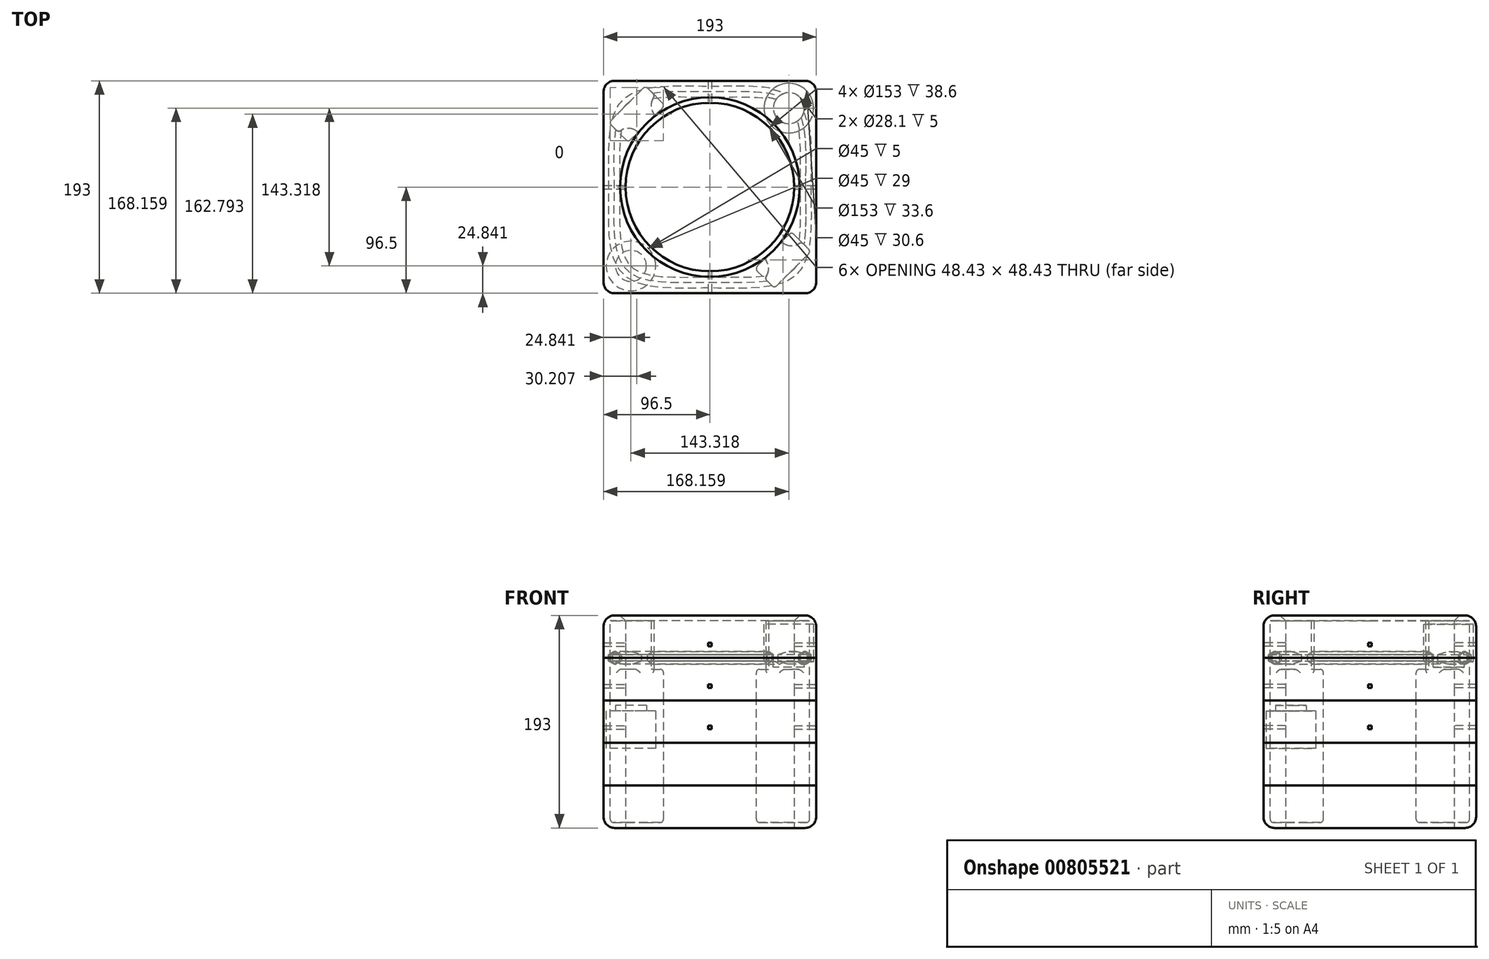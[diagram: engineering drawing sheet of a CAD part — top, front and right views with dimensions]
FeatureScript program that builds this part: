
annotation { "Feature Type Name" : "Feature", "Feature Type Description" : "" }
export const myFeature = defineFeature(function(context is Context, id is Id, definition is map)
    precondition{}
    {
        {
            var Q0;
            Q0=qCreatedBy(makeId("Top.planeOp"),FACE);
            cPlane(context, id + "F0", {"entities" : qUnion([Q0]), "cplaneType" : CPlaneType.OFFSET, "offset" : 0 * mm, "width" : 150 * mm, "height" : 150 * mm});
        }
        {
            var Q0;
            Q0=qCreatedBy(makeId("Top.planeOp"),FACE);
            cPlane(context, id + "F1", {"entities" : qUnion([Q0]), "cplaneType" : CPlaneType.OFFSET, "offset" : 38.6 * mm, "width" : 150 * mm, "height" : 150 * mm});
        }
        {
            var Q0;
            Q0=qCreatedBy(makeId("Top.planeOp"),FACE);
            cPlane(context, id + "F2", {"entities" : qUnion([Q0]), "cplaneType" : CPlaneType.OFFSET, "offset" : 77.2 * mm, "width" : 150 * mm, "height" : 150 * mm});
        }
        {
            var Q0;
            Q0=qCreatedBy(makeId("Top.planeOp"),FACE);
            cPlane(context, id + "F3", {"entities" : qUnion([Q0]), "cplaneType" : CPlaneType.OFFSET, "offset" : 115.8 * mm, "width" : 150 * mm, "height" : 150 * mm});
        }
        {
            var Q0;
            Q0=qCreatedBy(makeId("Top.planeOp"),FACE);
            cPlane(context, id + "F4", {"entities" : qUnion([Q0]), "cplaneType" : CPlaneType.OFFSET, "offset" : 154.4 * mm, "width" : 150 * mm, "height" : 150 * mm});
        }
        {
            var Q0;
            Q0=qCreatedBy(id+"F0.planeOp",FACE);
            cPlane(context, id + "F5", {"entities" : qUnion([Q0]), "cplaneType" : CPlaneType.OFFSET, "offset" : 5 * mm, "width" : 150 * mm, "height" : 150 * mm});
        }
        {
            var Q0;
            Q0=qCreatedBy(id+"F0.planeOp",FACE);
            var sketch = newSketch(context, id + "F6", { "sketchPlane" : qUnion([Q0])});
            skCircle(sketch, "E0", {"center": v(0, 0) * mm, "radius": 76.5 * mm});
            skLineSegment(sketch, "E1.bottom", {"start": v(96.5, 96.5) * mm, "end": v(-96.5, 96.5) * mm});
            skLineSegment(sketch, "E1.top", {"start": v(96.5, -96.5) * mm, "end": v(-96.5, -96.5) * mm});
            skLineSegment(sketch, "E1.left", {"start": v(96.5, 96.5) * mm, "end": v(96.5, -96.5) * mm});
            skLineSegment(sketch, "E1.right", {"start": v(-96.5, 96.5) * mm, "end": v(-96.5, -96.5) * mm});
            skLineSegment(sketch, "E2", {"start": v(-76.5, 0) * mm, "end": v(-96.5, 0) * mm, "construction": true});
            skPoint(sketch, "E2.startSnap0", {"position": v(-96.5, 0) * mm});
            skSolve(sketch);
        }
        {
            var Q0;
            Q0=qCreatedBy(id+"F1.planeOp",FACE);
            var sketch = newSketch(context, id + "F7", { "sketchPlane" : qUnion([Q0])});
            skCircle(sketch, "E3", {"center": v(0, 0) * mm, "radius": 76.5 * mm});
            skLineSegment(sketch, "E4.bottom", {"start": v(96.5, 96.5) * mm, "end": v(-96.5, 96.5) * mm});
            skLineSegment(sketch, "E4.top", {"start": v(96.5, -96.5) * mm, "end": v(-96.5, -96.5) * mm});
            skLineSegment(sketch, "E4.left", {"start": v(96.5, 96.5) * mm, "end": v(96.5, -96.5) * mm});
            skLineSegment(sketch, "E4.right", {"start": v(-96.5, 96.5) * mm, "end": v(-96.5, -96.5) * mm});
            skLineSegment(sketch, "E5", {"start": v(-76.5, 0) * mm, "end": v(-96.5, 0) * mm, "construction": true});
            skPoint(sketch, "E5.startSnap0", {"position": v(-96.5, 0) * mm});
            skSolve(sketch);
        }
        {
            var Q0;
            Q0=qCreatedBy(id+"F2.planeOp",FACE);
            var sketch = newSketch(context, id + "F8", { "sketchPlane" : qUnion([Q0])});
            skCircle(sketch, "E6", {"center": v(0, 0) * mm, "radius": 76.5 * mm});
            skLineSegment(sketch, "E7.bottom", {"start": v(96.5, 96.5) * mm, "end": v(-96.5, 96.5) * mm});
            skLineSegment(sketch, "E7.top", {"start": v(96.5, -96.5) * mm, "end": v(-96.5, -96.5) * mm});
            skLineSegment(sketch, "E7.left", {"start": v(96.5, 96.5) * mm, "end": v(96.5, -96.5) * mm});
            skLineSegment(sketch, "E7.right", {"start": v(-96.5, 96.5) * mm, "end": v(-96.5, -96.5) * mm});
            skLineSegment(sketch, "E8", {"start": v(-76.5, 0) * mm, "end": v(-96.5, 0) * mm, "construction": true});
            skPoint(sketch, "E8.startSnap0", {"position": v(-96.5, 0) * mm});
            skSolve(sketch);
        }
        {
            var Q0;
            Q0=qCreatedBy(id+"F3.planeOp",FACE);
            var sketch = newSketch(context, id + "F9", { "sketchPlane" : qUnion([Q0])});
            skCircle(sketch, "E9", {"center": v(0, 0) * mm, "radius": 76.5 * mm});
            skLineSegment(sketch, "E10.bottom", {"start": v(96.5, 96.5) * mm, "end": v(-96.5, 96.5) * mm});
            skLineSegment(sketch, "E10.top", {"start": v(96.5, -96.5) * mm, "end": v(-96.5, -96.5) * mm});
            skLineSegment(sketch, "E10.left", {"start": v(96.5, 96.5) * mm, "end": v(96.5, -96.5) * mm});
            skLineSegment(sketch, "E10.right", {"start": v(-96.5, 96.5) * mm, "end": v(-96.5, -96.5) * mm});
            skLineSegment(sketch, "E11", {"start": v(-76.5, 0) * mm, "end": v(-96.5, 0) * mm, "construction": true});
            skPoint(sketch, "E11.startSnap0", {"position": v(-96.5, 0) * mm});
            skSolve(sketch);
        }
        {
            var Q0;
            Q0=qCreatedBy(id+"F4.planeOp",FACE);
            var sketch = newSketch(context, id + "F10", { "sketchPlane" : qUnion([Q0])});
            skCircle(sketch, "E12", {"center": v(0, 0) * mm, "radius": 76.5 * mm});
            skLineSegment(sketch, "E13.bottom", {"start": v(96.5, 96.5) * mm, "end": v(-96.5, 96.5) * mm});
            skLineSegment(sketch, "E13.top", {"start": v(96.5, -96.5) * mm, "end": v(-96.5, -96.5) * mm});
            skLineSegment(sketch, "E13.left", {"start": v(96.5, 96.5) * mm, "end": v(96.5, -96.5) * mm});
            skLineSegment(sketch, "E13.right", {"start": v(-96.5, 96.5) * mm, "end": v(-96.5, -96.5) * mm});
            skLineSegment(sketch, "E14", {"start": v(-76.5, 0) * mm, "end": v(-96.5, 0) * mm, "construction": true});
            skPoint(sketch, "E14.startSnap0", {"position": v(-96.5, 0) * mm});
            skSolve(sketch);
        }
        {
            var Q0;
            Q0=qCreatedBy(id+"F5.planeOp",FACE);
            var sketch = newSketch(context, id + "F11", { "sketchPlane" : qUnion([Q0])});
            skCircle(sketch, "E15", {"center": v(0, 0) * mm, "radius": 76.5 * mm, "construction": true});
            skLineSegment(sketch, "E16.bottom", {"start": v(96.5, 96.5) * mm, "end": v(-96.5, 96.5) * mm, "construction": true});
            skLineSegment(sketch, "E16.top", {"start": v(96.5, -96.5) * mm, "end": v(-96.5, -96.5) * mm, "construction": true});
            skLineSegment(sketch, "E16.left", {"start": v(96.5, 96.5) * mm, "end": v(96.5, -96.5) * mm, "construction": true});
            skLineSegment(sketch, "E16.right", {"start": v(-96.5, 96.5) * mm, "end": v(-96.5, -96.5) * mm, "construction": true});
            skLineSegment(sketch, "E17", {"start": v(-57.45, 57.45) * mm, "end": v(-40.84, 74.07) * mm});
            skLineSegment(sketch, "E18", {"start": v(-57.45, 57.45) * mm, "end": v(-74.07, 40.84) * mm});
            skLineSegment(sketch, "E19", {"start": v(-74.07, 40.84) * mm, "end": v(-91.75, 58.51) * mm});
            skLineSegment(sketch, "E20", {"start": v(-76.5, 0) * mm, "end": v(-96.5, 0) * mm, "construction": true});
            skLineSegment(sketch, "E21", {"start": v(-91.75, 58.51) * mm, "end": v(-75.13, 75.13) * mm});
            skLineSegment(sketch, "E22", {"start": v(-75.13, 75.13) * mm, "end": v(-58.51, 91.75) * mm});
            skLineSegment(sketch, "E23", {"start": v(-58.51, 91.75) * mm, "end": v(-40.84, 74.07) * mm});
            skLineSegment(sketch, "E24", {"start": v(-91.75, 58.51) * mm, "end": v(-96.5, 58.51) * mm, "construction": true});
            skLineSegment(sketch, "E25", {"start": v(-58.51, 91.75) * mm, "end": v(-58.51, 96.5) * mm, "construction": true});
            skLineSegment(sketch, "E26", {"start": v(57.45, -57.45) * mm, "end": v(74.07, -40.84) * mm});
            skLineSegment(sketch, "E27", {"start": v(57.45, -57.45) * mm, "end": v(40.84, -74.07) * mm});
            skLineSegment(sketch, "E28", {"start": v(40.84, -74.07) * mm, "end": v(58.51, -91.75) * mm});
            skLineSegment(sketch, "E29", {"start": v(91.75, -58.51) * mm, "end": v(74.07, -40.84) * mm});
            skLineSegment(sketch, "E30", {"start": v(91.75, -58.51) * mm, "end": v(96.5, -58.51) * mm, "construction": true});
            skLineSegment(sketch, "E31", {"start": v(58.51, -91.75) * mm, "end": v(75.13, -75.13) * mm});
            skLineSegment(sketch, "E32", {"start": v(75.13, -75.13) * mm, "end": v(91.75, -58.51) * mm});
            skLineSegment(sketch, "E33", {"start": v(-57.45, 57.45) * mm, "end": v(-54.1, 54.1) * mm, "construction": true});
            skLineSegment(sketch, "E34", {"start": v(57.45, -57.45) * mm, "end": v(54.1, -54.1) * mm, "construction": true});
            skLineSegment(sketch, "E35", {"start": v(58.51, -91.75) * mm, "end": v(58.51, -96.5) * mm, "construction": true});
            skLineSegment(sketch, "E36", {"start": v(54.1, -54.1) * mm, "end": v(60.81, -54.1) * mm, "construction": true});
            skLineSegment(sketch, "E37", {"start": v(-54.1, 54.1) * mm, "end": v(-60.81, 54.1) * mm, "construction": true});
            skCircle(sketch, "E38", {"center": v(-74.07, 40.84) * mm, "radius": 12.5 * mm});
            skCircle(sketch, "E39", {"center": v(-40.84, 74.07) * mm, "radius": 12.5 * mm});
            skCircle(sketch, "E40", {"center": v(40.84, -74.07) * mm, "radius": 12.5 * mm});
            skCircle(sketch, "E41", {"center": v(74.07, -40.84) * mm, "radius": 12.5 * mm});
            skSolve(sketch);
        }
        {
            var Q0;
            Q0=makeQuery(id+"F6.imprint","IMPRINT",FACE,{"disambiguationData":[TD([[makeQuery(id+"F6.imprint","IMPRINT",EDGE,{"derivedFrom":sQuery(id+"F6.wireOp",EDGE,"E0")}),-1.0]])]});
            extrude(context, id + "F12", {"entities" : qUnion([Q0]), "depth" : 38.6 * mm, "offsetDistance" : 25 * mm});
        }
        {
            var Q0;
            Q0=makeQuery(id+"F7.imprint","IMPRINT",FACE,{"disambiguationData":[TD([[makeQuery(id+"F7.imprint","IMPRINT",EDGE,{"derivedFrom":sQuery(id+"F7.wireOp",EDGE,"E3")}),-1.0]])]});
            extrude(context, id + "F13", {"entities" : qUnion([Q0]), "depth" : 38.6 * mm, "offsetDistance" : 25 * mm});
        }
        {
            var Q0;
            Q0=makeQuery(id+"F8.imprint","IMPRINT",FACE,{"disambiguationData":[TD([[makeQuery(id+"F8.imprint","IMPRINT",EDGE,{"derivedFrom":sQuery(id+"F8.wireOp",EDGE,"E6")}),-1.0]])]});
            extrude(context, id + "F14", {"entities" : qUnion([Q0]), "depth" : 38.6 * mm, "offsetDistance" : 25 * mm});
        }
        {
            var Q0;
            Q0=makeQuery(id+"F9.imprint","IMPRINT",FACE,{"disambiguationData":[TD([[makeQuery(id+"F9.imprint","IMPRINT",EDGE,{"derivedFrom":sQuery(id+"F9.wireOp",EDGE,"E9")}),-1.0]])]});
            extrude(context, id + "F15", {"entities" : qUnion([Q0]), "depth" : 38.6 * mm, "offsetDistance" : 25 * mm});
        }
        {
            var Q0;
            Q0=makeQuery(id+"F10.imprint","IMPRINT",FACE,{"disambiguationData":[TD([[makeQuery(id+"F10.imprint","IMPRINT",EDGE,{"derivedFrom":sQuery(id+"F10.wireOp",EDGE,"E12")}),-1.0]])]});
            extrude(context, id + "F16", {"entities" : qUnion([Q0]), "depth" : 38.6 * mm, "offsetDistance" : 25 * mm});
        }
        {
            var Q0;
            Q0=makeQuery(id+"F16.opExtrude","CAP_FACE",FACE,{"disambiguationData":[OSD([sQuery(id+"F10.wireOp",EDGE,"E12"),sQuery(id+"F10.wireOp",EDGE,"E13.bottom"),sQuery(id+"F10.wireOp",EDGE,"E13.top"),sQuery(id+"F10.wireOp",EDGE,"E13.left"),sQuery(id+"F10.wireOp",EDGE,"E13.right")])],"isStart":false});
            cPlane(context, id + "F17", {"entities" : qUnion([Q0]), "cplaneType" : CPlaneType.OFFSET, "offset" : 8 * mm, "oppositeDirection" : true, "width" : 150 * mm, "height" : 150 * mm});
        }
        {
            var Q0;
            Q0=qCreatedBy(id+"F2.planeOp",FACE);
            cPlane(context, id + "F18", {"entities" : qUnion([Q0]), "cplaneType" : CPlaneType.OFFSET, "offset" : 5 * mm, "oppositeDirection" : true, "width" : 150 * mm, "height" : 150 * mm});
        }
        {
            var Q0;
            {var subQ0=sQuery(id+"F11.wireOp",EDGE,"E28");var subQ1=sQuery(id+"F11.wireOp",EDGE,"E27");var subQ2=makeQuery(id+"F11.imprint","INTERSECT",VERTEX,{"derivedFrom":[subQ1,subQ0]});Q0=makeQuery(id+"F11.imprint","IMPRINT",FACE,{"disambiguationData":[TD([[makeQuery(id+"F11.imprint","IMPRINT",EDGE,{"disambiguationData":[TD([[subQ2,1.0]])],"derivedFrom":subQ1}),1.0]])]});}
            var Q1;
            {var subQ0=sQuery(id+"F11.wireOp",EDGE,"E29");var subQ1=sQuery(id+"F11.wireOp",EDGE,"E26");var subQ2=makeQuery(id+"F11.imprint","INTERSECT",VERTEX,{"derivedFrom":[subQ1,subQ0]});Q1=makeQuery(id+"F11.imprint","IMPRINT",FACE,{"disambiguationData":[TD([[makeQuery(id+"F11.imprint","IMPRINT",EDGE,{"disambiguationData":[TD([[subQ2,1.0]])],"derivedFrom":subQ1}),-1.0]])]});}
            var Q2;
            {var subQ0=sQuery(id+"F11.wireOp",EDGE,"E19");var subQ1=sQuery(id+"F11.wireOp",EDGE,"E18");var subQ2=makeQuery(id+"F11.imprint","INTERSECT",VERTEX,{"derivedFrom":[subQ1,subQ0]});Q2=makeQuery(id+"F11.imprint","IMPRINT",FACE,{"disambiguationData":[TD([[makeQuery(id+"F11.imprint","IMPRINT",EDGE,{"disambiguationData":[TD([[subQ2,1.0]])],"derivedFrom":subQ1}),-1.0]])]});}
            var Q3;
            {var subQ0=sQuery(id+"F11.wireOp",EDGE,"E23");var subQ1=sQuery(id+"F11.wireOp",EDGE,"E17");var subQ2=makeQuery(id+"F11.imprint","INTERSECT",VERTEX,{"derivedFrom":[subQ1,subQ0]});Q3=makeQuery(id+"F11.imprint","IMPRINT",FACE,{"disambiguationData":[TD([[makeQuery(id+"F11.imprint","IMPRINT",EDGE,{"disambiguationData":[TD([[subQ2,1.0]])],"derivedFrom":subQ1}),1.0]])]});}
            extrude(context, id + "F19", {"entities" : qUnion([Q0, Q1, Q2, Q3]), "operationType" : NewBodyOperationType.REMOVE, "depth" : 139 * mm, "offsetDistance" : 25 * mm});
        }
        {
            var Q0;
            {var subQ0=sQuery(id+"F11.wireOp",EDGE,"E21");Q0=makeQuery(id+"F11.imprint","IMPRINT",FACE,{"disambiguationData":[TD([[makeQuery(id+"F11.imprint","IMPRINT",EDGE,{"derivedFrom":subQ0}),-1.0]])]});}
            var Q1;
            {var subQ9=sQuery(id+"F11.wireOp",EDGE,"E31");Q1=makeQuery(id+"F11.imprint","IMPRINT",FACE,{"disambiguationData":[TD([[makeQuery(id+"F11.imprint","IMPRINT",EDGE,{"derivedFrom":subQ9}),1.0]])]});}
            extrude(context, id + "F20", {"entities" : qUnion([Q0, Q1]), "operationType" : NewBodyOperationType.REMOVE, "depth" : 183 * mm, "offsetDistance" : 25 * mm});
        }
        {
            var Q0;
            Q0=makeQuery(id+"F16.opExtrude","SWEPT_FACE",FACE,{"disambiguationData":[OSD([sQuery(id+"F10.wireOp",EDGE,"E13.top")])]});
            var sketch = newSketch(context, id + "F21", { "sketchPlane" : qUnion([Q0])});
            skLineSegment(sketch, "E42", {"start": v(0, 193) * mm, "end": v(0, 154.4) * mm, "construction": true});
            skLineSegment(sketch, "E43.bottom", {"start": v(1.59, 168) * mm, "end": v(-1.59, 168) * mm});
            skLineSegment(sketch, "E43.top", {"start": v(1.59, 164.82) * mm, "end": v(-1.59, 164.82) * mm});
            skLineSegment(sketch, "E43.left", {"start": v(1.59, 168) * mm, "end": v(1.59, 164.82) * mm});
            skLineSegment(sketch, "E43.right", {"start": v(-1.59, 168) * mm, "end": v(-1.59, 164.82) * mm});
            skPoint(sketch, "E43.middle", {"position": v(0, 166.41) * mm});
            skLineSegment(sketch, "E44", {"start": v(0, 154.4) * mm, "end": v(0, 0) * mm, "construction": true});
            skLineSegment(sketch, "E45.bottom", {"start": v(1.59, 130.42) * mm, "end": v(-1.59, 130.42) * mm});
            skLineSegment(sketch, "E45.top", {"start": v(1.59, 127.25) * mm, "end": v(-1.59, 127.25) * mm});
            skLineSegment(sketch, "E45.left", {"start": v(1.59, 130.42) * mm, "end": v(1.59, 127.25) * mm});
            skLineSegment(sketch, "E45.right", {"start": v(-1.59, 130.42) * mm, "end": v(-1.59, 127.25) * mm});
            skPoint(sketch, "E45.middle", {"position": v(0, 128.84) * mm});
            skLineSegment(sketch, "E46.bottom", {"start": v(1.59, 92.85) * mm, "end": v(-1.59, 92.85) * mm});
            skLineSegment(sketch, "E46.top", {"start": v(1.59, 89.67) * mm, "end": v(-1.59, 89.67) * mm});
            skLineSegment(sketch, "E46.left", {"start": v(1.59, 92.85) * mm, "end": v(1.59, 89.67) * mm});
            skLineSegment(sketch, "E46.right", {"start": v(-1.59, 92.85) * mm, "end": v(-1.59, 89.67) * mm});
            skPoint(sketch, "E46.middle", {"position": v(0, 91.26) * mm});
            skSolve(sketch);
        }
        {
            var Q0;
            Q0=makeQuery(id+"F16.opExtrude","SWEPT_FACE",FACE,{"disambiguationData":[OSD([sQuery(id+"F10.wireOp",EDGE,"E13.left")])]});
            var sketch = newSketch(context, id + "F22", { "sketchPlane" : qUnion([Q0])});
            skLineSegment(sketch, "E47.bottom", {"start": v(1.59, 168) * mm, "end": v(-1.59, 168) * mm});
            skLineSegment(sketch, "E47.top", {"start": v(1.59, 164.82) * mm, "end": v(-1.59, 164.82) * mm});
            skLineSegment(sketch, "E47.left", {"start": v(1.59, 168) * mm, "end": v(1.59, 164.82) * mm});
            skLineSegment(sketch, "E47.right", {"start": v(-1.59, 168) * mm, "end": v(-1.59, 164.82) * mm});
            skPoint(sketch, "E47.middle", {"position": v(0, 166.41) * mm});
            skLineSegment(sketch, "E48", {"start": v(0, 193) * mm, "end": v(0, 0) * mm, "construction": true});
            skLineSegment(sketch, "E49.bottom", {"start": v(1.59, 130.43) * mm, "end": v(-1.59, 130.43) * mm});
            skLineSegment(sketch, "E49.top", {"start": v(1.59, 127.25) * mm, "end": v(-1.59, 127.25) * mm});
            skLineSegment(sketch, "E49.left", {"start": v(1.59, 130.43) * mm, "end": v(1.59, 127.25) * mm});
            skLineSegment(sketch, "E49.right", {"start": v(-1.59, 130.43) * mm, "end": v(-1.59, 127.25) * mm});
            skPoint(sketch, "E49.middle", {"position": v(0, 128.84) * mm});
            skLineSegment(sketch, "E50.bottom", {"start": v(1.59, 92.85) * mm, "end": v(-1.59, 92.85) * mm});
            skLineSegment(sketch, "E50.top", {"start": v(1.59, 89.68) * mm, "end": v(-1.59, 89.68) * mm});
            skLineSegment(sketch, "E50.left", {"start": v(1.59, 92.85) * mm, "end": v(1.59, 89.68) * mm});
            skLineSegment(sketch, "E50.right", {"start": v(-1.59, 92.85) * mm, "end": v(-1.59, 89.68) * mm});
            skPoint(sketch, "E50.middle", {"position": v(0, 91.26) * mm});
            skSolve(sketch);
        }
        {
            var Q0;
            Q0=makeQuery(id+"F21.imprint","IMPRINT",FACE,{"disambiguationData":[TD([[makeQuery(id+"F21.imprint","IMPRINT",EDGE,{"derivedFrom":sQuery(id+"F21.wireOp",EDGE,"E43.bottom")}),1.0]])]});
            var Q1;
            Q1=makeQuery(id+"F21.imprint","IMPRINT",FACE,{"disambiguationData":[TD([[makeQuery(id+"F21.imprint","IMPRINT",EDGE,{"derivedFrom":sQuery(id+"F21.wireOp",EDGE,"E45.bottom")}),1.0]])]});
            var Q2;
            Q2=makeQuery(id+"F21.imprint","IMPRINT",FACE,{"disambiguationData":[TD([[makeQuery(id+"F21.imprint","IMPRINT",EDGE,{"derivedFrom":sQuery(id+"F21.wireOp",EDGE,"E46.bottom")}),1.0]])]});
            extrude(context, id + "F23", {"entities" : qUnion([Q0, Q1, Q2]), "operationType" : NewBodyOperationType.REMOVE, "oppositeDirection" : true, "depth" : 193 * mm, "offsetDistance" : 25 * mm});
        }
        {
            var Q0;
            Q0=makeQuery(id+"F22.imprint","IMPRINT",FACE,{"disambiguationData":[TD([[makeQuery(id+"F22.imprint","IMPRINT",EDGE,{"derivedFrom":sQuery(id+"F22.wireOp",EDGE,"E47.bottom")}),1.0]])]});
            var Q1;
            Q1=makeQuery(id+"F22.imprint","IMPRINT",FACE,{"disambiguationData":[TD([[makeQuery(id+"F22.imprint","IMPRINT",EDGE,{"derivedFrom":sQuery(id+"F22.wireOp",EDGE,"E49.bottom")}),1.0]])]});
            var Q2;
            Q2=makeQuery(id+"F22.imprint","IMPRINT",FACE,{"disambiguationData":[TD([[makeQuery(id+"F22.imprint","IMPRINT",EDGE,{"derivedFrom":sQuery(id+"F22.wireOp",EDGE,"E50.bottom")}),1.0]])]});
            extrude(context, id + "F24", {"entities" : qUnion([Q0, Q1, Q2]), "operationType" : NewBodyOperationType.REMOVE, "oppositeDirection" : true, "depth" : 193 * mm, "offsetDistance" : 25 * mm});
        }
        {
            var Q0;
            Q0=qCreatedBy(id+"F4.planeOp",FACE);
            cPlane(context, id + "F25", {"entities" : qUnion([Q0]), "cplaneType" : CPlaneType.OFFSET, "offset" : 24.9 * mm, "oppositeDirection" : true, "width" : 150 * mm, "height" : 150 * mm});
        }
        {
            var Q0;
            Q0=qCreatedBy(id+"F25.planeOp",FACE);
            var sketch = newSketch(context, id + "F26", { "sketchPlane" : qUnion([Q0])});
            skCircle(sketch, "E51", {"center": v(0, 0) * mm, "radius": 76.5 * mm, "construction": true});
            skLineSegment(sketch, "E52.bottom", {"start": v(96.5, 96.5) * mm, "end": v(-96.5, 96.5) * mm, "construction": true});
            skLineSegment(sketch, "E52.top", {"start": v(96.5, -96.5) * mm, "end": v(-96.5, -96.5) * mm, "construction": true});
            skLineSegment(sketch, "E52.left", {"start": v(96.5, 96.5) * mm, "end": v(96.5, -96.5) * mm, "construction": true});
            skLineSegment(sketch, "E52.right", {"start": v(-96.5, 96.5) * mm, "end": v(-96.5, -96.5) * mm, "construction": true});
            skLineSegment(sketch, "E53", {"start": v(-76.5, 0) * mm, "end": v(-96.5, 0) * mm});
            skLineSegment(sketch, "E54", {"start": v(-96.5, 96.5) * mm, "end": v(-54.1, 54.1) * mm});
            skLineSegment(sketch, "E55", {"start": v(54.1, 54.1) * mm, "end": v(96.5, 96.5) * mm});
            skLineSegment(sketch, "E56", {"start": v(76.5, 0) * mm, "end": v(96.5, 0) * mm});
            skLineSegment(sketch, "E57", {"start": v(54.1, -54.1) * mm, "end": v(96.5, -96.5) * mm});
            skLineSegment(sketch, "E58", {"start": v(0, -76.5) * mm, "end": v(0, -96.5) * mm});
            skLineSegment(sketch, "E59", {"start": v(-54.1, -54.1) * mm, "end": v(-96.5, -96.5) * mm});
            skPoint(sketch, "E60", {"position": v(75.3, 75.3) * mm});
            skPoint(sketch, "E61", {"position": v(-75.3, 75.3) * mm});
            skPoint(sketch, "E62", {"position": v(-75.3, -75.3) * mm});
            skPoint(sketch, "E63", {"position": v(75.3, -75.3) * mm});
            skPoint(sketch, "E64", {"position": v(0, -86.5) * mm});
            skPoint(sketch, "E65", {"position": v(86.5, 0) * mm});
            skPoint(sketch, "E66", {"position": v(-86.5, 0) * mm});
            skLineSegment(sketch, "E67", {"start": v(0, 76.5) * mm, "end": v(0, 96.5) * mm});
            skPoint(sketch, "E68", {"position": v(0, 86.5) * mm});
            skFitSpline(sketch, "E69", {"points": [v(-75.3, 75.3) * mm, v(0, 86.5) * mm, v(75.3, 75.3) * mm, v(86.5, 0) * mm, v(75.3, -75.3) * mm, v(0, -86.5) * mm, v(-75.3, -75.3) * mm, v(-86.5, 0) * mm, v(-75.3, 75.3) * mm]});
            skSolve(sketch);
        }
        {
            var Q0;
            Q0=sQuery(id+"F26.wireOp",EDGE,"E56");
            cPoint(context, id + "F27", {"entities" : qUnion([Q0]), "parameter" : 0.5});
        }
        {
            var Q0;
            Q0=qCreatedBy(id+"F27",VERTEX);
            var Q1;
            Q1=sQuery(id+"F26.wireOp",EDGE,"E69");
            cPlane(context, id + "F28", {"entities" : qUnion([Q0, Q1]), "cplaneType" : CPlaneType.CURVE_POINT, "offset" : 25 * mm, "width" : 150 * mm, "height" : 150 * mm});
        }
        {
            var Q0;
            Q0=qCreatedBy(id+"F28.planeOp",FACE);
            var sketch = newSketch(context, id + "F29", { "sketchPlane" : qUnion([Q0])});
            skCircle(sketch, "E70.cCircle", {"center": v(86.71, 154.47) * mm, "radius": 5 * mm, "construction": true});
            skLineSegment(sketch, "E70.0", {"start": v(91.71, 157.35) * mm, "end": v(91.71, 151.58) * mm});
            skLineSegment(sketch, "E70.1", {"start": v(91.71, 151.58) * mm, "end": v(86.71, 148.7) * mm});
            skLineSegment(sketch, "E70.2", {"start": v(86.71, 148.7) * mm, "end": v(81.71, 151.58) * mm});
            skLineSegment(sketch, "E70.3", {"start": v(81.71, 151.58) * mm, "end": v(81.71, 157.35) * mm});
            skLineSegment(sketch, "E70.4", {"start": v(81.71, 157.35) * mm, "end": v(86.71, 160.24) * mm});
            skLineSegment(sketch, "E70.5", {"start": v(86.71, 160.24) * mm, "end": v(91.71, 157.35) * mm});
            skPoint(sketch, "E70.0.midPoint", {"position": v(91.71, 154.47) * mm});
            skSolve(sketch);
        }
        {
            var Q0;
            Q0=makeQuery(id+"F29.imprint","IMPRINT",FACE,{"disambiguationData":[TD([[makeQuery(id+"F29.imprint","IMPRINT",EDGE,{"derivedFrom":sQuery(id+"F29.wireOp",EDGE,"E70.0")}),-1.0]])]});
            var Q1;
            Q1=sQuery(id+"F26.wireOp",EDGE,"E69");
            sweep(context, id + "F30", {"operationType" : NewBodyOperationType.REMOVE, "profiles" : qUnion([Q0]), "path" : qUnion([Q1])});
        }
        {
            var Q0;
            Q0=qCreatedBy(id+"F18.planeOp",FACE);
            var sketch = newSketch(context, id + "F31", { "sketchPlane" : qUnion([Q0])});
            skCircle(sketch, "E71", {"center": v(0, 0) * mm, "radius": 76.5 * mm, "construction": true});
            skLineSegment(sketch, "E72.bottom", {"start": v(96.5, 96.5) * mm, "end": v(-96.5, 96.5) * mm, "construction": true});
            skLineSegment(sketch, "E72.top", {"start": v(96.5, -96.5) * mm, "end": v(-96.5, -96.5) * mm, "construction": true});
            skLineSegment(sketch, "E72.left", {"start": v(96.5, 96.5) * mm, "end": v(96.5, -96.5) * mm, "construction": true});
            skLineSegment(sketch, "E72.right", {"start": v(-96.5, 96.5) * mm, "end": v(-96.5, -96.5) * mm, "construction": true});
            skLineSegment(sketch, "E73", {"start": v(-76.5, 0) * mm, "end": v(-96.5, 0) * mm, "construction": true});
            skCircle(sketch, "E74", {"center": v(-71.66, -71.66) * mm, "radius": 22.5 * mm});
            skLineSegment(sketch, "E75", {"start": v(-71.66, -71.66) * mm, "end": v(-96.5, -71.66) * mm, "construction": true});
            skLineSegment(sketch, "E76", {"start": v(-71.66, -71.66) * mm, "end": v(-71.66, -96.5) * mm, "construction": true});
            skLineSegment(sketch, "E77", {"start": v(-71.66, -71.66) * mm, "end": v(-54.1, -54.1) * mm, "construction": true});
            skCircle(sketch, "E78", {"center": v(-71.66, -71.66) * mm, "radius": 14.05 * mm});
            skLineSegment(sketch, "E79", {"start": v(-71.66, -71.66) * mm, "end": v(-71.66, -62.16) * mm, "construction": true});
            skLineSegment(sketch, "E80", {"start": v(-71.66, -71.66) * mm, "end": v(-71.66, -81.16) * mm, "construction": true});
            skLineSegment(sketch, "E81", {"start": v(-71.66, -71.66) * mm, "end": v(-63.66, -71.66) * mm, "construction": true});
            skLineSegment(sketch, "E82", {"start": v(-71.66, -71.66) * mm, "end": v(-79.66, -71.66) * mm, "construction": true});
            skCircle(sketch, "E83", {"center": v(-71.66, -62.16) * mm, "radius": 1.55 * mm});
            skCircle(sketch, "E84", {"center": v(-79.66, -71.66) * mm, "radius": 1.55 * mm});
            skCircle(sketch, "E85", {"center": v(-71.66, -81.16) * mm, "radius": 1.55 * mm});
            skCircle(sketch, "E86", {"center": v(-63.66, -71.66) * mm, "radius": 1.55 * mm});
            skLineSegment(sketch, "E87", {"start": v(0, 0) * mm, "end": v(-54.1, -54.1) * mm, "construction": true});
            skSolve(sketch);
        }
        {
            var Q0;
            Q0=qCreatedBy(id+"F17.planeOp",FACE);
            var sketch = newSketch(context, id + "F32", { "sketchPlane" : qUnion([Q0])});
            skCircle(sketch, "E88", {"center": v(0, 0) * mm, "radius": 76.5 * mm, "construction": true});
            skLineSegment(sketch, "E89.bottom", {"start": v(-96.5, 96.5) * mm, "end": v(96.5, 96.5) * mm, "construction": true});
            skLineSegment(sketch, "E89.top", {"start": v(-96.5, -96.5) * mm, "end": v(96.5, -96.5) * mm, "construction": true});
            skLineSegment(sketch, "E89.left", {"start": v(-96.5, 96.5) * mm, "end": v(-96.5, -96.5) * mm, "construction": true});
            skLineSegment(sketch, "E89.right", {"start": v(96.5, 96.5) * mm, "end": v(96.5, -96.5) * mm, "construction": true});
            skLineSegment(sketch, "E90", {"start": v(-76.5, 0) * mm, "end": v(-96.5, 0) * mm, "construction": true});
            skCircle(sketch, "E91", {"center": v(71.66, 71.66) * mm, "radius": 22.5 * mm});
            skCircle(sketch, "E92", {"center": v(71.66, 71.66) * mm, "radius": 14.05 * mm});
            skLineSegment(sketch, "E93", {"start": v(71.66, 71.66) * mm, "end": v(54.1, 54.1) * mm, "construction": true});
            skLineSegment(sketch, "E94", {"start": v(71.66, 71.66) * mm, "end": v(71.66, 96.5) * mm, "construction": true});
            skLineSegment(sketch, "E95", {"start": v(71.66, 71.66) * mm, "end": v(96.5, 71.66) * mm, "construction": true});
            skLineSegment(sketch, "E96", {"start": v(0, 0) * mm, "end": v(54.1, 54.1) * mm, "construction": true});
            skLineSegment(sketch, "E97", {"start": v(71.66, 71.66) * mm, "end": v(71.66, 62.16) * mm, "construction": true});
            skPoint(sketch, "E98", {"position": v(79.66, 71.66) * mm});
            skPoint(sketch, "E99", {"position": v(71.66, 81.16) * mm});
            skLineSegment(sketch, "E100", {"start": v(71.66, 71.66) * mm, "end": v(63.66, 71.66) * mm, "construction": true});
            skCircle(sketch, "E101", {"center": v(71.66, 81.16) * mm, "radius": 1.55 * mm});
            skCircle(sketch, "E102", {"center": v(79.66, 71.66) * mm, "radius": 1.55 * mm});
            skCircle(sketch, "E103", {"center": v(63.66, 71.66) * mm, "radius": 1.55 * mm});
            skCircle(sketch, "E104", {"center": v(71.66, 62.16) * mm, "radius": 1.55 * mm});
            skSolve(sketch);
        }
        {
            var Q0;
            Q0=makeQuery(id+"F31.imprint","IMPRINT",FACE,{"disambiguationData":[TD([[makeQuery(id+"F31.imprint","IMPRINT",EDGE,{"derivedFrom":sQuery(id+"F31.wireOp",EDGE,"E74")}),1.0]])]});
            var Q1;
            Q1=makeQuery(id+"F31.imprint","IMPRINT",FACE,{"disambiguationData":[TD([[makeQuery(id+"F31.imprint","IMPRINT",EDGE,{"derivedFrom":sQuery(id+"F31.wireOp",EDGE,"E86")}),1.0]])]});
            var Q2;
            Q2=makeQuery(id+"F31.imprint","IMPRINT",FACE,{"disambiguationData":[TD([[makeQuery(id+"F31.imprint","IMPRINT",EDGE,{"derivedFrom":sQuery(id+"F31.wireOp",EDGE,"E83")}),1.0]])]});
            var Q3;
            Q3=makeQuery(id+"F31.imprint","IMPRINT",FACE,{"disambiguationData":[TD([[makeQuery(id+"F31.imprint","IMPRINT",EDGE,{"derivedFrom":sQuery(id+"F31.wireOp",EDGE,"E85")}),1.0]])]});
            var Q4;
            Q4=makeQuery(id+"F31.imprint","IMPRINT",FACE,{"disambiguationData":[TD([[makeQuery(id+"F31.imprint","IMPRINT",EDGE,{"derivedFrom":sQuery(id+"F31.wireOp",EDGE,"E78")}),1.0]])]});
            var Q5;
            Q5=makeQuery(id+"F31.imprint","IMPRINT",FACE,{"disambiguationData":[TD([[makeQuery(id+"F31.imprint","IMPRINT",EDGE,{"derivedFrom":sQuery(id+"F31.wireOp",EDGE,"E84")}),1.0]])]});
            extrude(context, id + "F33", {"entities" : qUnion([Q0, Q1, Q2, Q3, Q4, Q5]), "operationType" : NewBodyOperationType.REMOVE, "depth" : 34 * mm, "offsetDistance" : 25 * mm});
        }
        {
            var Q0;
            Q0=makeQuery(id+"F31.imprint","IMPRINT",FACE,{"disambiguationData":[TD([[makeQuery(id+"F31.imprint","IMPRINT",EDGE,{"derivedFrom":sQuery(id+"F31.wireOp",EDGE,"E84")}),1.0]])]});
            var Q1;
            Q1=makeQuery(id+"F31.imprint","IMPRINT",FACE,{"disambiguationData":[TD([[makeQuery(id+"F31.imprint","IMPRINT",EDGE,{"derivedFrom":sQuery(id+"F31.wireOp",EDGE,"E83")}),1.0]])]});
            var Q2;
            Q2=makeQuery(id+"F31.imprint","IMPRINT",FACE,{"disambiguationData":[TD([[makeQuery(id+"F31.imprint","IMPRINT",EDGE,{"derivedFrom":sQuery(id+"F31.wireOp",EDGE,"E86")}),1.0]])]});
            var Q3;
            Q3=makeQuery(id+"F31.imprint","IMPRINT",FACE,{"disambiguationData":[TD([[makeQuery(id+"F31.imprint","IMPRINT",EDGE,{"derivedFrom":sQuery(id+"F31.wireOp",EDGE,"E85")}),1.0]])]});
            var Q4;
            Q4=makeQuery(id+"F31.imprint","IMPRINT",FACE,{"disambiguationData":[TD([[makeQuery(id+"F31.imprint","IMPRINT",EDGE,{"derivedFrom":sQuery(id+"F31.wireOp",EDGE,"E78")}),1.0]])]});
            extrude(context, id + "F34", {"entities" : qUnion([Q0, Q1, Q2, Q3, Q4]), "operationType" : NewBodyOperationType.REMOVE, "depth" : 39 * mm, "offsetDistance" : 25 * mm});
        }
        {
            var Q0;
            Q0=makeQuery(id+"F32.imprint","IMPRINT",FACE,{"disambiguationData":[TD([[makeQuery(id+"F32.imprint","IMPRINT",EDGE,{"derivedFrom":sQuery(id+"F32.wireOp",EDGE,"E102")}),1.0]])]});
            var Q1;
            Q1=makeQuery(id+"F32.imprint","IMPRINT",FACE,{"disambiguationData":[TD([[makeQuery(id+"F32.imprint","IMPRINT",EDGE,{"derivedFrom":sQuery(id+"F32.wireOp",EDGE,"E101")}),1.0]])]});
            var Q2;
            Q2=makeQuery(id+"F32.imprint","IMPRINT",FACE,{"disambiguationData":[TD([[makeQuery(id+"F32.imprint","IMPRINT",EDGE,{"derivedFrom":sQuery(id+"F32.wireOp",EDGE,"E104")}),1.0]])]});
            var Q3;
            Q3=makeQuery(id+"F32.imprint","IMPRINT",FACE,{"disambiguationData":[TD([[makeQuery(id+"F32.imprint","IMPRINT",EDGE,{"derivedFrom":sQuery(id+"F32.wireOp",EDGE,"E103")}),1.0]])]});
            var Q4;
            Q4=makeQuery(id+"F32.imprint","IMPRINT",FACE,{"disambiguationData":[TD([[makeQuery(id+"F32.imprint","IMPRINT",EDGE,{"derivedFrom":sQuery(id+"F32.wireOp",EDGE,"E92")}),1.0]])]});
            extrude(context, id + "F35", {"entities" : qUnion([Q0, Q1, Q2, Q3, Q4]), "operationType" : NewBodyOperationType.REMOVE, "oppositeDirection" : true, "depth" : 39 * mm, "offsetDistance" : 25 * mm});
        }
        {
            var Q0;
            Q0=makeQuery(id+"F32.imprint","IMPRINT",FACE,{"disambiguationData":[TD([[makeQuery(id+"F32.imprint","IMPRINT",EDGE,{"derivedFrom":sQuery(id+"F32.wireOp",EDGE,"E104")}),1.0]])]});
            var Q1;
            Q1=makeQuery(id+"F32.imprint","IMPRINT",FACE,{"disambiguationData":[TD([[makeQuery(id+"F32.imprint","IMPRINT",EDGE,{"derivedFrom":sQuery(id+"F32.wireOp",EDGE,"E103")}),1.0]])]});
            var Q2;
            Q2=makeQuery(id+"F32.imprint","IMPRINT",FACE,{"disambiguationData":[TD([[makeQuery(id+"F32.imprint","IMPRINT",EDGE,{"derivedFrom":sQuery(id+"F32.wireOp",EDGE,"E101")}),1.0]])]});
            var Q3;
            Q3=makeQuery(id+"F32.imprint","IMPRINT",FACE,{"disambiguationData":[TD([[makeQuery(id+"F32.imprint","IMPRINT",EDGE,{"derivedFrom":sQuery(id+"F32.wireOp",EDGE,"E102")}),1.0]])]});
            var Q4;
            Q4=makeQuery(id+"F32.imprint","IMPRINT",FACE,{"disambiguationData":[TD([[makeQuery(id+"F32.imprint","IMPRINT",EDGE,{"derivedFrom":sQuery(id+"F32.wireOp",EDGE,"E92")}),1.0]])]});
            var Q5;
            Q5=makeQuery(id+"F32.imprint","IMPRINT",FACE,{"disambiguationData":[TD([[makeQuery(id+"F32.imprint","IMPRINT",EDGE,{"derivedFrom":sQuery(id+"F32.wireOp",EDGE,"E91")}),1.0]])]});
            extrude(context, id + "F36", {"entities" : qUnion([Q0, Q1, Q2, Q3, Q4, Q5]), "operationType" : NewBodyOperationType.REMOVE, "oppositeDirection" : true, "depth" : 34 * mm, "offsetDistance" : 25 * mm});
        }
        {
            var Q0;
            Q0=makeQuery(id+"F32.imprint","IMPRINT",FACE,{"disambiguationData":[TD([[makeQuery(id+"F32.imprint","IMPRINT",EDGE,{"derivedFrom":sQuery(id+"F32.wireOp",EDGE,"E102")}),1.0]])]});
            var Q1;
            Q1=makeQuery(id+"F32.imprint","IMPRINT",FACE,{"disambiguationData":[TD([[makeQuery(id+"F32.imprint","IMPRINT",EDGE,{"derivedFrom":sQuery(id+"F32.wireOp",EDGE,"E101")}),1.0]])]});
            var Q2;
            Q2=makeQuery(id+"F32.imprint","IMPRINT",FACE,{"disambiguationData":[TD([[makeQuery(id+"F32.imprint","IMPRINT",EDGE,{"derivedFrom":sQuery(id+"F32.wireOp",EDGE,"E103")}),1.0]])]});
            var Q3;
            Q3=makeQuery(id+"F32.imprint","IMPRINT",FACE,{"disambiguationData":[TD([[makeQuery(id+"F32.imprint","IMPRINT",EDGE,{"derivedFrom":sQuery(id+"F32.wireOp",EDGE,"E104")}),1.0]])]});
            var Q4;
            Q4=makeQuery(id+"F32.imprint","IMPRINT",FACE,{"disambiguationData":[TD([[makeQuery(id+"F32.imprint","IMPRINT",EDGE,{"derivedFrom":sQuery(id+"F32.wireOp",EDGE,"E92")}),1.0]])]});
            var Q5;
            Q5=makeQuery(id+"F32.imprint","IMPRINT",FACE,{"disambiguationData":[TD([[makeQuery(id+"F32.imprint","IMPRINT",EDGE,{"derivedFrom":sQuery(id+"F32.wireOp",EDGE,"E91")}),1.0]])]});
            extrude(context, id + "F37", {"entities" : qUnion([Q0, Q1, Q2, Q3, Q4, Q5]), "operationType" : NewBodyOperationType.REMOVE, "oppositeDirection" : true, "depth" : 15 * mm, "offsetDistance" : 25 * mm});
        }
        {
            var Q0;
            Q0=makeQuery(id+"F16.opExtrude","SWEPT_EDGE",EDGE,{"disambiguationData":[OSD([sQuery(id+"F10.wireOp",EDGE,"E13.top"),sQuery(id+"F10.wireOp",EDGE,"E13.right")])]});
            var Q1;
            Q1=makeQuery(id+"F15.opExtrude","SWEPT_EDGE",EDGE,{"disambiguationData":[OSD([sQuery(id+"F9.wireOp",EDGE,"E10.top"),sQuery(id+"F9.wireOp",EDGE,"E10.right")])]});
            var Q2;
            Q2=makeQuery(id+"F16.opExtrude","SWEPT_EDGE",EDGE,{"disambiguationData":[OSD([sQuery(id+"F10.wireOp",EDGE,"E13.top"),sQuery(id+"F10.wireOp",EDGE,"E13.left")])]});
            var Q3;
            Q3=makeQuery(id+"F15.opExtrude","SWEPT_EDGE",EDGE,{"disambiguationData":[OSD([sQuery(id+"F9.wireOp",EDGE,"E10.top"),sQuery(id+"F9.wireOp",EDGE,"E10.left")])]});
            var Q4;
            Q4=makeQuery(id+"F16.opExtrude","SWEPT_EDGE",EDGE,{"disambiguationData":[OSD([sQuery(id+"F10.wireOp",EDGE,"E13.bottom"),sQuery(id+"F10.wireOp",EDGE,"E13.left")])]});
            var Q5;
            Q5=makeQuery(id+"F15.opExtrude","SWEPT_EDGE",EDGE,{"disambiguationData":[OSD([sQuery(id+"F9.wireOp",EDGE,"E10.bottom"),sQuery(id+"F9.wireOp",EDGE,"E10.left")])]});
            var Q6;
            Q6=makeQuery(id+"F15.opExtrude","SWEPT_EDGE",EDGE,{"disambiguationData":[OSD([sQuery(id+"F9.wireOp",EDGE,"E10.bottom"),sQuery(id+"F9.wireOp",EDGE,"E10.right")])]});
            var Q7;
            Q7=makeQuery(id+"F16.opExtrude","SWEPT_EDGE",EDGE,{"disambiguationData":[OSD([sQuery(id+"F10.wireOp",EDGE,"E13.bottom"),sQuery(id+"F10.wireOp",EDGE,"E13.right")])]});
            var Q8;
            Q8=makeQuery(id+"F16.opExtrude","CAP_EDGE",EDGE,{"disambiguationData":[OSD([sQuery(id+"F10.wireOp",EDGE,"E13.right")])],"isStart":false});
            var Q9;
            Q9=makeQuery(id+"F16.opExtrude","CAP_EDGE",EDGE,{"disambiguationData":[OSD([sQuery(id+"F10.wireOp",EDGE,"E13.bottom")])],"isStart":false});
            var Q10;
            Q10=makeQuery(id+"F16.opExtrude","CAP_EDGE",EDGE,{"disambiguationData":[OSD([sQuery(id+"F10.wireOp",EDGE,"E13.left")])],"isStart":false});
            var Q11;
            Q11=makeQuery(id+"F16.opExtrude","CAP_EDGE",EDGE,{"disambiguationData":[OSD([sQuery(id+"F10.wireOp",EDGE,"E13.top")])],"isStart":false});
            var Q12;
            Q12=makeQuery(id+"F14.opExtrude","SWEPT_EDGE",EDGE,{"disambiguationData":[OSD([sQuery(id+"F8.wireOp",EDGE,"E7.top"),sQuery(id+"F8.wireOp",EDGE,"E7.left")])]});
            var Q13;
            Q13=makeQuery(id+"F13.opExtrude","SWEPT_EDGE",EDGE,{"disambiguationData":[OSD([sQuery(id+"F7.wireOp",EDGE,"E4.top"),sQuery(id+"F7.wireOp",EDGE,"E4.left")])]});
            var Q14;
            Q14=makeQuery(id+"F12.opExtrude","SWEPT_EDGE",EDGE,{"disambiguationData":[OSD([sQuery(id+"F6.wireOp",EDGE,"E1.top"),sQuery(id+"F6.wireOp",EDGE,"E1.left")])]});
            var Q15;
            Q15=makeQuery(id+"F12.opExtrude","SWEPT_EDGE",EDGE,{"disambiguationData":[OSD([sQuery(id+"F6.wireOp",EDGE,"E1.top"),sQuery(id+"F6.wireOp",EDGE,"E1.right")])]});
            var Q16;
            Q16=makeQuery(id+"F13.opExtrude","SWEPT_EDGE",EDGE,{"disambiguationData":[OSD([sQuery(id+"F7.wireOp",EDGE,"E4.top"),sQuery(id+"F7.wireOp",EDGE,"E4.right")])]});
            var Q17;
            Q17=makeQuery(id+"F14.opExtrude","SWEPT_EDGE",EDGE,{"disambiguationData":[OSD([sQuery(id+"F8.wireOp",EDGE,"E7.top"),sQuery(id+"F8.wireOp",EDGE,"E7.right")])]});
            var Q18;
            Q18=makeQuery(id+"F14.opExtrude","SWEPT_EDGE",EDGE,{"disambiguationData":[OSD([sQuery(id+"F8.wireOp",EDGE,"E7.bottom"),sQuery(id+"F8.wireOp",EDGE,"E7.left")])]});
            var Q19;
            Q19=makeQuery(id+"F13.opExtrude","SWEPT_EDGE",EDGE,{"disambiguationData":[OSD([sQuery(id+"F7.wireOp",EDGE,"E4.bottom"),sQuery(id+"F7.wireOp",EDGE,"E4.left")])]});
            var Q20;
            Q20=makeQuery(id+"F12.opExtrude","SWEPT_EDGE",EDGE,{"disambiguationData":[OSD([sQuery(id+"F6.wireOp",EDGE,"E1.bottom"),sQuery(id+"F6.wireOp",EDGE,"E1.left")])]});
            var Q21;
            Q21=makeQuery(id+"F14.opExtrude","SWEPT_EDGE",EDGE,{"disambiguationData":[OSD([sQuery(id+"F8.wireOp",EDGE,"E7.bottom"),sQuery(id+"F8.wireOp",EDGE,"E7.right")])]});
            var Q22;
            Q22=makeQuery(id+"F13.opExtrude","SWEPT_EDGE",EDGE,{"disambiguationData":[OSD([sQuery(id+"F7.wireOp",EDGE,"E4.bottom"),sQuery(id+"F7.wireOp",EDGE,"E4.right")])]});
            var Q23;
            Q23=makeQuery(id+"F12.opExtrude","SWEPT_EDGE",EDGE,{"disambiguationData":[OSD([sQuery(id+"F6.wireOp",EDGE,"E1.bottom"),sQuery(id+"F6.wireOp",EDGE,"E1.right")])]});
            var Q24;
            Q24=makeQuery(id+"F12.opExtrude","CAP_EDGE",EDGE,{"disambiguationData":[OSD([sQuery(id+"F6.wireOp",EDGE,"E1.left")])],"isStart":true});
            var Q25;
            Q25=makeQuery(id+"F12.opExtrude","CAP_EDGE",EDGE,{"disambiguationData":[OSD([sQuery(id+"F6.wireOp",EDGE,"E1.bottom")])],"isStart":true});
            var Q26;
            Q26=makeQuery(id+"F12.opExtrude","CAP_EDGE",EDGE,{"disambiguationData":[OSD([sQuery(id+"F6.wireOp",EDGE,"E1.right")])],"isStart":true});
            var Q27;
            Q27=makeQuery(id+"F12.opExtrude","CAP_EDGE",EDGE,{"disambiguationData":[OSD([sQuery(id+"F6.wireOp",EDGE,"E1.top")])],"isStart":true});
            fillet(context, id + "F38", {"entities" : qUnion([Q0, Q1, Q2, Q3, Q4, Q5, Q6, Q7, Q8, Q9, Q10, Q11, Q12, Q13, Q14, Q15, Q16, Q17, Q18, Q19, Q20, Q21, Q22, Q23, Q24, Q25, Q26, Q27]), "radius" : 10 * mm, "tangentPropagation" : true, "allowEdgeOverflow" : false});
        }
        {
            var Q0;
            Q0=makeQuery(id+"F16.opExtrude","CAP_EDGE",EDGE,{"disambiguationData":[OSD([sQuery(id+"F10.wireOp",EDGE,"E12")])],"isStart":false});
            chamfer(context, id + "F39", {"entities" : qUnion([Q0]), "width" : 5 * mm, "tangentPropagation" : true});
        }
        {
            var Q0;
            {var subQ0=sQuery(id+"F11.wireOp",EDGE,"E26");var subQ1=sQuery(id+"F11.wireOp",EDGE,"E29");Q0=makeQuery(id+"F19.boolean.opBoolean","COPY",EDGE,{"disambiguationData":[TD([makeQuery(id+"F19.opExtrude","CAP_FACE",FACE,{"disambiguationData":[OSD([subQ0,subQ1,sQuery(id+"F11.wireOp",EDGE,"E41")])],"isStart":false})])],"derivedFrom":makeQuery(id+"F19.opExtrude","SWEPT_EDGE",EDGE,{"disambiguationData":[OSD([subQ0,subQ1])]})});}
            var Q1;
            Q1=makeQuery(id+"F19.boolean.opBoolean","COPY",EDGE,{"derivedFrom":makeQuery(id+"F19.opExtrude","CAP_EDGE",EDGE,{"disambiguationData":[OSD([sQuery(id+"F11.wireOp",EDGE,"E26")])],"isStart":false})});
            var Q2;
            Q2=makeQuery(id+"F19.boolean.opBoolean","COPY",EDGE,{"derivedFrom":makeQuery(id+"F19.opExtrude","CAP_EDGE",EDGE,{"disambiguationData":[OSD([sQuery(id+"F11.wireOp",EDGE,"E29")])],"isStart":false})});
            var Q3;
            {var subQ0=sQuery(id+"F11.wireOp",EDGE,"E41");var subQ1=sQuery(id+"F11.wireOp",EDGE,"E26");var subQ2=sQuery(id+"F11.wireOp",EDGE,"E29");var subQ3=sQuery(id+"F11.wireOp",EDGE,"E32");Q3=makeQuery(id+"F20.boolean.opBoolean","COPY",EDGE,{"disambiguationData":[topologyDisambiguationEdgeConnected([makeQuery(id+"F19.boolean.opBoolean","COPY",FACE,{"disambiguationData":[TD([makeQuery(id+"F19.opExtrude","CAP_FACE",FACE,{"disambiguationData":[OSD([subQ1,subQ2,subQ0])],"isStart":false})])],"derivedFrom":makeQuery(id+"F19.opExtrude","SWEPT_FACE",FACE,{"disambiguationData":[OSD([subQ2])]})}),makeQuery(id+"F20.opExtrude","SWEPT_FACE",FACE,{"disambiguationData":[OSD([subQ2])]}),makeQuery(id+"F20.opExtrude","SWEPT_FACE",FACE,{"disambiguationData":[OSD([sQuery(id+"F11.wireOp",EDGE,"E31"),subQ3])]})])],"derivedFrom":makeQuery(id+"F20.opExtrude","SWEPT_EDGE",EDGE,{"disambiguationData":[OSD([subQ2,subQ3])]})});}
            var Q4;
            {var subQ0=sQuery(id+"F11.wireOp",EDGE,"E29");var subQ1=sQuery(id+"F11.wireOp",EDGE,"E32");Q4=makeQuery(id+"F20.boolean.opBoolean","COPY",EDGE,{"disambiguationData":[topologyDisambiguationEdgeConnected([makeQuery(id+"F20.opExtrude","SWEPT_FACE",FACE,{"disambiguationData":[OSD([subQ0])]}),makeQuery(id+"F20.opExtrude","SWEPT_FACE",FACE,{"disambiguationData":[OSD([sQuery(id+"F11.wireOp",EDGE,"E31"),subQ1])]})])],"derivedFrom":makeQuery(id+"F20.opExtrude","SWEPT_EDGE",EDGE,{"disambiguationData":[OSD([subQ0,subQ1])]})});}
            var Q5;
            {var subQ0=sQuery(id+"F11.wireOp",EDGE,"E41");var subQ1=sQuery(id+"F11.wireOp",EDGE,"E26");var subQ2=sQuery(id+"F11.wireOp",EDGE,"E29");Q5=makeQuery(id+"F20.boolean.opBoolean","COPY",EDGE,{"disambiguationData":[topologyDisambiguationEdgeConnected([makeQuery(id+"F19.boolean.opBoolean","COPY",FACE,{"disambiguationData":[TD([makeQuery(id+"F19.opExtrude","CAP_FACE",FACE,{"disambiguationData":[OSD([subQ1,subQ2,subQ0])],"isStart":false})])],"derivedFrom":makeQuery(id+"F19.opExtrude","SWEPT_FACE",FACE,{"disambiguationData":[OSD([subQ2])]})}),makeQuery(id+"F20.opExtrude","SWEPT_FACE",FACE,{"disambiguationData":[OSD([subQ2])]}),makeQuery(id+"F20.opExtrude","SWEPT_FACE",FACE,{"disambiguationData":[OSD([subQ0])]})])],"derivedFrom":makeQuery(id+"F20.opExtrude","SWEPT_EDGE",EDGE,{"disambiguationData":[OSD([subQ2,subQ0])]})});}
            var Q6;
            {var subQ0=sQuery(id+"F11.wireOp",EDGE,"E29");var subQ1=sQuery(id+"F11.wireOp",EDGE,"E41");Q6=makeQuery(id+"F20.boolean.opBoolean","COPY",EDGE,{"disambiguationData":[topologyDisambiguationEdgeConnected([makeQuery(id+"F20.opExtrude","SWEPT_FACE",FACE,{"disambiguationData":[OSD([subQ0])]}),makeQuery(id+"F20.opExtrude","SWEPT_FACE",FACE,{"disambiguationData":[OSD([subQ1])]})])],"derivedFrom":makeQuery(id+"F20.opExtrude","SWEPT_EDGE",EDGE,{"disambiguationData":[OSD([subQ0,subQ1])]})});}
            var Q7;
            {var subQ1=sQuery(id+"F11.wireOp",EDGE,"E41");var subQ2=sQuery(id+"F11.wireOp",EDGE,"E29");var subQ3=sQuery(id+"F11.wireOp",EDGE,"E26");var subQ4=sQuery(id+"F11.wireOp",EDGE,"E28");var subQ5=sQuery(id+"F11.wireOp",EDGE,"E40");var subQ6=sQuery(id+"F11.wireOp",EDGE,"E27");Q7=makeQuery(id+"F20.boolean.opBoolean","COPY",EDGE,{"disambiguationData":[topologyDisambiguationEdgeConnected([makeQuery(id+"F19.boolean.opBoolean","COPY",FACE,{"disambiguationData":[TD([makeQuery(id+"F19.opExtrude","CAP_FACE",FACE,{"disambiguationData":[OSD([subQ3,subQ2,subQ1])],"isStart":false})])],"derivedFrom":makeQuery(id+"F19.opExtrude","SWEPT_FACE",FACE,{"disambiguationData":[OSD([subQ3])]})}),makeQuery(id+"F19.boolean.opBoolean","COPY",FACE,{"disambiguationData":[TD([makeQuery(id+"F19.opExtrude","CAP_FACE",FACE,{"disambiguationData":[OSD([subQ6,subQ4,subQ5])],"isStart":false})])],"derivedFrom":makeQuery(id+"F19.opExtrude","SWEPT_FACE",FACE,{"disambiguationData":[OSD([subQ6])]})}),makeQuery(id+"F20.opExtrude","SWEPT_FACE",FACE,{"disambiguationData":[OSD([subQ3,subQ6])]}),makeQuery(id+"F20.opExtrude","SWEPT_FACE",FACE,{"disambiguationData":[OSD([subQ1])]})])],"derivedFrom":makeQuery(id+"F20.opExtrude","SWEPT_EDGE",EDGE,{"disambiguationData":[OSD([subQ3,subQ1])]})});}
            var Q8;
            {var subQ0=sQuery(id+"F11.wireOp",EDGE,"E26");var subQ1=sQuery(id+"F11.wireOp",EDGE,"E41");Q8=makeQuery(id+"F20.boolean.opBoolean","COPY",EDGE,{"disambiguationData":[topologyDisambiguationEdgeConnected([makeQuery(id+"F20.opExtrude","SWEPT_FACE",FACE,{"disambiguationData":[OSD([subQ0,sQuery(id+"F11.wireOp",EDGE,"E27")])]}),makeQuery(id+"F20.opExtrude","SWEPT_FACE",FACE,{"disambiguationData":[OSD([subQ1])]})])],"derivedFrom":makeQuery(id+"F20.opExtrude","SWEPT_EDGE",EDGE,{"disambiguationData":[OSD([subQ0,subQ1])]})});}
            var Q9;
            {var subQ0=sQuery(id+"F11.wireOp",EDGE,"E28");var subQ1=sQuery(id+"F11.wireOp",EDGE,"E27");Q9=makeQuery(id+"F19.boolean.opBoolean","COPY",EDGE,{"disambiguationData":[TD([makeQuery(id+"F19.opExtrude","CAP_FACE",FACE,{"disambiguationData":[OSD([subQ1,subQ0,sQuery(id+"F11.wireOp",EDGE,"E40")])],"isStart":false})])],"derivedFrom":makeQuery(id+"F19.opExtrude","SWEPT_EDGE",EDGE,{"disambiguationData":[OSD([subQ1,subQ0])]})});}
            var Q10;
            Q10=makeQuery(id+"F19.boolean.opBoolean","COPY",EDGE,{"derivedFrom":makeQuery(id+"F19.opExtrude","CAP_EDGE",EDGE,{"disambiguationData":[OSD([sQuery(id+"F11.wireOp",EDGE,"E27")])],"isStart":false})});
            var Q11;
            Q11=makeQuery(id+"F19.boolean.opBoolean","COPY",EDGE,{"derivedFrom":makeQuery(id+"F19.opExtrude","CAP_EDGE",EDGE,{"disambiguationData":[OSD([sQuery(id+"F11.wireOp",EDGE,"E28")])],"isStart":false})});
            var Q12;
            {var subQ0=sQuery(id+"F11.wireOp",EDGE,"E27");var subQ1=sQuery(id+"F11.wireOp",EDGE,"E40");Q12=makeQuery(id+"F20.boolean.opBoolean","COPY",EDGE,{"disambiguationData":[topologyDisambiguationEdgeConnected([makeQuery(id+"F20.opExtrude","SWEPT_FACE",FACE,{"disambiguationData":[OSD([sQuery(id+"F11.wireOp",EDGE,"E26"),subQ0])]}),makeQuery(id+"F20.opExtrude","SWEPT_FACE",FACE,{"disambiguationData":[OSD([subQ1])]})])],"derivedFrom":makeQuery(id+"F20.opExtrude","SWEPT_EDGE",EDGE,{"disambiguationData":[OSD([subQ0,subQ1])]})});}
            var Q13;
            {var subQ1=sQuery(id+"F11.wireOp",EDGE,"E41");var subQ2=sQuery(id+"F11.wireOp",EDGE,"E29");var subQ3=sQuery(id+"F11.wireOp",EDGE,"E26");var subQ4=sQuery(id+"F11.wireOp",EDGE,"E28");var subQ5=sQuery(id+"F11.wireOp",EDGE,"E40");var subQ6=sQuery(id+"F11.wireOp",EDGE,"E27");Q13=makeQuery(id+"F20.boolean.opBoolean","COPY",EDGE,{"disambiguationData":[topologyDisambiguationEdgeConnected([makeQuery(id+"F19.boolean.opBoolean","COPY",FACE,{"disambiguationData":[TD([makeQuery(id+"F19.opExtrude","CAP_FACE",FACE,{"disambiguationData":[OSD([subQ3,subQ2,subQ1])],"isStart":false})])],"derivedFrom":makeQuery(id+"F19.opExtrude","SWEPT_FACE",FACE,{"disambiguationData":[OSD([subQ3])]})}),makeQuery(id+"F19.boolean.opBoolean","COPY",FACE,{"disambiguationData":[TD([makeQuery(id+"F19.opExtrude","CAP_FACE",FACE,{"disambiguationData":[OSD([subQ6,subQ4,subQ5])],"isStart":false})])],"derivedFrom":makeQuery(id+"F19.opExtrude","SWEPT_FACE",FACE,{"disambiguationData":[OSD([subQ6])]})}),makeQuery(id+"F20.opExtrude","SWEPT_FACE",FACE,{"disambiguationData":[OSD([subQ3,subQ6])]}),makeQuery(id+"F20.opExtrude","SWEPT_FACE",FACE,{"disambiguationData":[OSD([subQ5])]})])],"derivedFrom":makeQuery(id+"F20.opExtrude","SWEPT_EDGE",EDGE,{"disambiguationData":[OSD([subQ6,subQ5])]})});}
            var Q14;
            {var subQ0=sQuery(id+"F11.wireOp",EDGE,"E27");var subQ1=sQuery(id+"F11.wireOp",EDGE,"E40");var subQ2=sQuery(id+"F11.wireOp",EDGE,"E28");Q14=makeQuery(id+"F20.boolean.opBoolean","COPY",EDGE,{"disambiguationData":[topologyDisambiguationEdgeConnected([makeQuery(id+"F19.boolean.opBoolean","COPY",FACE,{"disambiguationData":[TD([makeQuery(id+"F19.opExtrude","CAP_FACE",FACE,{"disambiguationData":[OSD([subQ0,subQ2,subQ1])],"isStart":false})])],"derivedFrom":makeQuery(id+"F19.opExtrude","SWEPT_FACE",FACE,{"disambiguationData":[OSD([subQ2])]})}),makeQuery(id+"F20.opExtrude","SWEPT_FACE",FACE,{"disambiguationData":[OSD([subQ2])]}),makeQuery(id+"F20.opExtrude","SWEPT_FACE",FACE,{"disambiguationData":[OSD([subQ1])]})])],"derivedFrom":makeQuery(id+"F20.opExtrude","SWEPT_EDGE",EDGE,{"disambiguationData":[OSD([subQ2,subQ1])]})});}
            var Q15;
            {var subQ0=sQuery(id+"F11.wireOp",EDGE,"E28");var subQ1=sQuery(id+"F11.wireOp",EDGE,"E40");Q15=makeQuery(id+"F20.boolean.opBoolean","COPY",EDGE,{"disambiguationData":[topologyDisambiguationEdgeConnected([makeQuery(id+"F20.opExtrude","SWEPT_FACE",FACE,{"disambiguationData":[OSD([subQ0])]}),makeQuery(id+"F20.opExtrude","SWEPT_FACE",FACE,{"disambiguationData":[OSD([subQ1])]})])],"derivedFrom":makeQuery(id+"F20.opExtrude","SWEPT_EDGE",EDGE,{"disambiguationData":[OSD([subQ0,subQ1])]})});}
            var Q16;
            {var subQ0=sQuery(id+"F11.wireOp",EDGE,"E28");var subQ1=sQuery(id+"F11.wireOp",EDGE,"E31");Q16=makeQuery(id+"F20.boolean.opBoolean","COPY",EDGE,{"disambiguationData":[topologyDisambiguationEdgeConnected([makeQuery(id+"F20.opExtrude","SWEPT_FACE",FACE,{"disambiguationData":[OSD([subQ0])]}),makeQuery(id+"F20.opExtrude","SWEPT_FACE",FACE,{"disambiguationData":[OSD([subQ1,sQuery(id+"F11.wireOp",EDGE,"E32")])]})])],"derivedFrom":makeQuery(id+"F20.opExtrude","SWEPT_EDGE",EDGE,{"disambiguationData":[OSD([subQ0,subQ1])]})});}
            var Q17;
            {var subQ0=sQuery(id+"F11.wireOp",EDGE,"E27");var subQ1=sQuery(id+"F11.wireOp",EDGE,"E40");var subQ2=sQuery(id+"F11.wireOp",EDGE,"E28");var subQ3=sQuery(id+"F11.wireOp",EDGE,"E31");Q17=makeQuery(id+"F20.boolean.opBoolean","COPY",EDGE,{"disambiguationData":[topologyDisambiguationEdgeConnected([makeQuery(id+"F19.boolean.opBoolean","COPY",FACE,{"disambiguationData":[TD([makeQuery(id+"F19.opExtrude","CAP_FACE",FACE,{"disambiguationData":[OSD([subQ0,subQ2,subQ1])],"isStart":false})])],"derivedFrom":makeQuery(id+"F19.opExtrude","SWEPT_FACE",FACE,{"disambiguationData":[OSD([subQ2])]})}),makeQuery(id+"F20.opExtrude","SWEPT_FACE",FACE,{"disambiguationData":[OSD([subQ2])]}),makeQuery(id+"F20.opExtrude","SWEPT_FACE",FACE,{"disambiguationData":[OSD([subQ3,sQuery(id+"F11.wireOp",EDGE,"E32")])]})])],"derivedFrom":makeQuery(id+"F20.opExtrude","SWEPT_EDGE",EDGE,{"disambiguationData":[OSD([subQ2,subQ3])]})});}
            var Q18;
            {var subQ0=sQuery(id+"F8.wireOp",EDGE,"E7.right");var subQ1=sQuery(id+"F8.wireOp",EDGE,"E7.left");var subQ2=sQuery(id+"F8.wireOp",EDGE,"E7.top");var subQ3=sQuery(id+"F8.wireOp",EDGE,"E7.bottom");var subQ4=sQuery(id+"F8.wireOp",EDGE,"E6");var subQ5=sQuery(id+"F11.wireOp",EDGE,"E28");var subQ6=sQuery(id+"F11.wireOp",EDGE,"E27");Q18=makeQuery(id+"F19.boolean.opBoolean","COPY",EDGE,{"disambiguationData":[TD([makeQuery(id+"F14.opExtrude","CAP_FACE",FACE,{"disambiguationData":[OSD([subQ4,subQ3,subQ2,subQ1,subQ0])],"isStart":true})])],"derivedFrom":makeQuery(id+"F19.opExtrude","SWEPT_EDGE",EDGE,{"disambiguationData":[OSD([subQ6,subQ5])]})});}
            var Q19;
            {var subQ0=sQuery(id+"F8.wireOp",EDGE,"E7.right");var subQ1=sQuery(id+"F8.wireOp",EDGE,"E7.left");var subQ2=sQuery(id+"F8.wireOp",EDGE,"E7.top");var subQ3=sQuery(id+"F8.wireOp",EDGE,"E7.bottom");var subQ4=sQuery(id+"F8.wireOp",EDGE,"E6");var subQ5=sQuery(id+"F11.wireOp",EDGE,"E26");var subQ6=sQuery(id+"F11.wireOp",EDGE,"E29");Q19=makeQuery(id+"F19.boolean.opBoolean","COPY",EDGE,{"disambiguationData":[TD([makeQuery(id+"F14.opExtrude","CAP_FACE",FACE,{"disambiguationData":[OSD([subQ4,subQ3,subQ2,subQ1,subQ0])],"isStart":true})])],"derivedFrom":makeQuery(id+"F19.opExtrude","SWEPT_EDGE",EDGE,{"disambiguationData":[OSD([subQ5,subQ6])]})});}
            var Q20;
            {var subQ0=sQuery(id+"F8.wireOp",EDGE,"E7.right");var subQ1=sQuery(id+"F8.wireOp",EDGE,"E7.left");var subQ2=sQuery(id+"F8.wireOp",EDGE,"E7.top");var subQ3=sQuery(id+"F8.wireOp",EDGE,"E7.bottom");var subQ4=sQuery(id+"F8.wireOp",EDGE,"E6");var subQ5=sQuery(id+"F11.wireOp",EDGE,"E29");var subQ6=sQuery(id+"F11.wireOp",EDGE,"E32");Q20=makeQuery(id+"F20.boolean.opBoolean","COPY",EDGE,{"disambiguationData":[topologyDisambiguationEdgeConnected([makeQuery(id+"F19.boolean.opBoolean","COPY",FACE,{"disambiguationData":[TD([makeQuery(id+"F14.opExtrude","CAP_FACE",FACE,{"disambiguationData":[OSD([subQ4,subQ3,subQ2,subQ1,subQ0])],"isStart":true})])],"derivedFrom":makeQuery(id+"F19.opExtrude","SWEPT_FACE",FACE,{"disambiguationData":[OSD([subQ5])]})}),makeQuery(id+"F20.opExtrude","SWEPT_FACE",FACE,{"disambiguationData":[OSD([subQ5])]}),makeQuery(id+"F20.opExtrude","SWEPT_FACE",FACE,{"disambiguationData":[OSD([sQuery(id+"F11.wireOp",EDGE,"E31"),subQ6])]})])],"derivedFrom":makeQuery(id+"F20.opExtrude","SWEPT_EDGE",EDGE,{"disambiguationData":[OSD([subQ5,subQ6])]})});}
            var Q21;
            {var subQ0=sQuery(id+"F8.wireOp",EDGE,"E7.right");var subQ1=sQuery(id+"F8.wireOp",EDGE,"E7.left");var subQ2=sQuery(id+"F8.wireOp",EDGE,"E7.top");var subQ3=sQuery(id+"F8.wireOp",EDGE,"E7.bottom");var subQ4=sQuery(id+"F8.wireOp",EDGE,"E6");var subQ5=sQuery(id+"F11.wireOp",EDGE,"E28");var subQ6=sQuery(id+"F11.wireOp",EDGE,"E31");Q21=makeQuery(id+"F20.boolean.opBoolean","COPY",EDGE,{"disambiguationData":[topologyDisambiguationEdgeConnected([makeQuery(id+"F19.boolean.opBoolean","COPY",FACE,{"disambiguationData":[TD([makeQuery(id+"F14.opExtrude","CAP_FACE",FACE,{"disambiguationData":[OSD([subQ4,subQ3,subQ2,subQ1,subQ0])],"isStart":true})])],"derivedFrom":makeQuery(id+"F19.opExtrude","SWEPT_FACE",FACE,{"disambiguationData":[OSD([subQ5])]})}),makeQuery(id+"F20.opExtrude","SWEPT_FACE",FACE,{"disambiguationData":[OSD([subQ5])]}),makeQuery(id+"F20.opExtrude","SWEPT_FACE",FACE,{"disambiguationData":[OSD([subQ6,sQuery(id+"F11.wireOp",EDGE,"E32")])]})])],"derivedFrom":makeQuery(id+"F20.opExtrude","SWEPT_EDGE",EDGE,{"disambiguationData":[OSD([subQ5,subQ6])]})});}
            var Q22;
            {var subQ0=sQuery(id+"F7.wireOp",EDGE,"E4.right");var subQ1=sQuery(id+"F7.wireOp",EDGE,"E4.left");var subQ2=sQuery(id+"F7.wireOp",EDGE,"E4.top");var subQ3=sQuery(id+"F7.wireOp",EDGE,"E4.bottom");var subQ4=sQuery(id+"F7.wireOp",EDGE,"E3");var subQ5=sQuery(id+"F11.wireOp",EDGE,"E28");var subQ6=sQuery(id+"F11.wireOp",EDGE,"E31");Q22=makeQuery(id+"F20.boolean.opBoolean","COPY",EDGE,{"disambiguationData":[topologyDisambiguationEdgeConnected([makeQuery(id+"F19.boolean.opBoolean","COPY",FACE,{"disambiguationData":[TD([makeQuery(id+"F13.opExtrude","CAP_FACE",FACE,{"disambiguationData":[OSD([subQ4,subQ3,subQ2,subQ1,subQ0])],"isStart":true})])],"derivedFrom":makeQuery(id+"F19.opExtrude","SWEPT_FACE",FACE,{"disambiguationData":[OSD([subQ5])]})}),makeQuery(id+"F20.opExtrude","SWEPT_FACE",FACE,{"disambiguationData":[OSD([subQ5])]}),makeQuery(id+"F20.opExtrude","SWEPT_FACE",FACE,{"disambiguationData":[OSD([subQ6,sQuery(id+"F11.wireOp",EDGE,"E32")])]})])],"derivedFrom":makeQuery(id+"F20.opExtrude","SWEPT_EDGE",EDGE,{"disambiguationData":[OSD([subQ5,subQ6])]})});}
            var Q23;
            {var subQ0=sQuery(id+"F7.wireOp",EDGE,"E4.right");var subQ1=sQuery(id+"F7.wireOp",EDGE,"E4.left");var subQ2=sQuery(id+"F7.wireOp",EDGE,"E4.top");var subQ3=sQuery(id+"F7.wireOp",EDGE,"E4.bottom");var subQ4=sQuery(id+"F7.wireOp",EDGE,"E3");var subQ5=sQuery(id+"F11.wireOp",EDGE,"E27");var subQ6=sQuery(id+"F11.wireOp",EDGE,"E28");Q23=makeQuery(id+"F19.boolean.opBoolean","COPY",EDGE,{"disambiguationData":[TD([makeQuery(id+"F13.opExtrude","CAP_FACE",FACE,{"disambiguationData":[OSD([subQ4,subQ3,subQ2,subQ1,subQ0])],"isStart":true})])],"derivedFrom":makeQuery(id+"F19.opExtrude","SWEPT_EDGE",EDGE,{"disambiguationData":[OSD([subQ5,subQ6])]})});}
            var Q24;
            {var subQ0=sQuery(id+"F7.wireOp",EDGE,"E4.right");var subQ1=sQuery(id+"F7.wireOp",EDGE,"E4.left");var subQ2=sQuery(id+"F7.wireOp",EDGE,"E4.top");var subQ3=sQuery(id+"F7.wireOp",EDGE,"E4.bottom");var subQ4=sQuery(id+"F7.wireOp",EDGE,"E3");var subQ5=sQuery(id+"F11.wireOp",EDGE,"E29");var subQ6=sQuery(id+"F11.wireOp",EDGE,"E32");Q24=makeQuery(id+"F20.boolean.opBoolean","COPY",EDGE,{"disambiguationData":[topologyDisambiguationEdgeConnected([makeQuery(id+"F19.boolean.opBoolean","COPY",FACE,{"disambiguationData":[TD([makeQuery(id+"F13.opExtrude","CAP_FACE",FACE,{"disambiguationData":[OSD([subQ4,subQ3,subQ2,subQ1,subQ0])],"isStart":true})])],"derivedFrom":makeQuery(id+"F19.opExtrude","SWEPT_FACE",FACE,{"disambiguationData":[OSD([subQ5])]})}),makeQuery(id+"F20.opExtrude","SWEPT_FACE",FACE,{"disambiguationData":[OSD([subQ5])]}),makeQuery(id+"F20.opExtrude","SWEPT_FACE",FACE,{"disambiguationData":[OSD([sQuery(id+"F11.wireOp",EDGE,"E31"),subQ6])]})])],"derivedFrom":makeQuery(id+"F20.opExtrude","SWEPT_EDGE",EDGE,{"disambiguationData":[OSD([subQ5,subQ6])]})});}
            var Q25;
            {var subQ0=sQuery(id+"F7.wireOp",EDGE,"E4.right");var subQ1=sQuery(id+"F7.wireOp",EDGE,"E4.left");var subQ2=sQuery(id+"F7.wireOp",EDGE,"E4.top");var subQ3=sQuery(id+"F7.wireOp",EDGE,"E4.bottom");var subQ4=sQuery(id+"F7.wireOp",EDGE,"E3");var subQ5=sQuery(id+"F11.wireOp",EDGE,"E26");var subQ6=sQuery(id+"F11.wireOp",EDGE,"E29");Q25=makeQuery(id+"F19.boolean.opBoolean","COPY",EDGE,{"disambiguationData":[TD([makeQuery(id+"F13.opExtrude","CAP_FACE",FACE,{"disambiguationData":[OSD([subQ4,subQ3,subQ2,subQ1,subQ0])],"isStart":true})])],"derivedFrom":makeQuery(id+"F19.opExtrude","SWEPT_EDGE",EDGE,{"disambiguationData":[OSD([subQ5,subQ6])]})});}
            var Q26;
            {var subQ0=sQuery(id+"F11.wireOp",EDGE,"E26");var subQ1=sQuery(id+"F11.wireOp",EDGE,"E29");Q26=makeQuery(id+"F19.boolean.opBoolean","COPY",EDGE,{"disambiguationData":[TD([makeQuery(id+"F19.opExtrude","CAP_FACE",FACE,{"disambiguationData":[OSD([subQ0,subQ1,sQuery(id+"F11.wireOp",EDGE,"E41")])],"isStart":true})])],"derivedFrom":makeQuery(id+"F19.opExtrude","SWEPT_EDGE",EDGE,{"disambiguationData":[OSD([subQ0,subQ1])]})});}
            var Q27;
            {var subQ0=sQuery(id+"F11.wireOp",EDGE,"E27");var subQ1=sQuery(id+"F11.wireOp",EDGE,"E26");Q27=makeQuery(id+"F20.boolean.opBoolean","MERGE",EDGE,{"derivedFrom":[makeQuery(id+"F19.boolean.opBoolean","COPY",EDGE,{"derivedFrom":makeQuery(id+"F19.opExtrude","CAP_EDGE",EDGE,{"disambiguationData":[OSD([subQ1])],"isStart":true})}),makeQuery(id+"F19.boolean.opBoolean","COPY",EDGE,{"derivedFrom":makeQuery(id+"F19.opExtrude","CAP_EDGE",EDGE,{"disambiguationData":[OSD([subQ0])],"isStart":true})}),makeQuery(id+"F20.opExtrude","CAP_EDGE",EDGE,{"disambiguationData":[OSD([subQ1,subQ0])],"isStart":true})]});}
            var Q28;
            {var subQ0=sQuery(id+"F11.wireOp",EDGE,"E28");var subQ1=sQuery(id+"F11.wireOp",EDGE,"E27");Q28=makeQuery(id+"F19.boolean.opBoolean","COPY",EDGE,{"disambiguationData":[TD([makeQuery(id+"F19.opExtrude","CAP_FACE",FACE,{"disambiguationData":[OSD([subQ1,subQ0,sQuery(id+"F11.wireOp",EDGE,"E40")])],"isStart":true})])],"derivedFrom":makeQuery(id+"F19.opExtrude","SWEPT_EDGE",EDGE,{"disambiguationData":[OSD([subQ1,subQ0])]})});}
            var Q29;
            {var subQ0=sQuery(id+"F11.wireOp",EDGE,"E28");Q29=makeQuery(id+"F20.boolean.opBoolean","MERGE",EDGE,{"derivedFrom":[makeQuery(id+"F19.boolean.opBoolean","COPY",EDGE,{"derivedFrom":makeQuery(id+"F19.opExtrude","CAP_EDGE",EDGE,{"disambiguationData":[OSD([subQ0])],"isStart":true})}),makeQuery(id+"F20.opExtrude","CAP_EDGE",EDGE,{"disambiguationData":[OSD([subQ0])],"isStart":true})]});}
            var Q30;
            Q30=makeQuery(id+"F20.boolean.opBoolean","COPY",EDGE,{"derivedFrom":makeQuery(id+"F20.opExtrude","CAP_EDGE",EDGE,{"disambiguationData":[OSD([sQuery(id+"F11.wireOp",EDGE,"E31"),sQuery(id+"F11.wireOp",EDGE,"E32")])],"isStart":true})});
            var Q31;
            {var subQ0=sQuery(id+"F11.wireOp",EDGE,"E40");var subQ1=sQuery(id+"F11.wireOp",EDGE,"E28");var subQ2=sQuery(id+"F11.wireOp",EDGE,"E27");var subQ3=sQuery(id+"F11.wireOp",EDGE,"E31");Q31=makeQuery(id+"F20.boolean.opBoolean","COPY",EDGE,{"disambiguationData":[topologyDisambiguationEdgeConnected([makeQuery(id+"F19.boolean.opBoolean","COPY",FACE,{"disambiguationData":[TD([makeQuery(id+"F19.opExtrude","CAP_FACE",FACE,{"disambiguationData":[OSD([subQ2,subQ1,subQ0])],"isStart":true})])],"derivedFrom":makeQuery(id+"F19.opExtrude","SWEPT_FACE",FACE,{"disambiguationData":[OSD([subQ1])]})}),makeQuery(id+"F20.opExtrude","SWEPT_FACE",FACE,{"disambiguationData":[OSD([subQ1])]}),makeQuery(id+"F20.opExtrude","SWEPT_FACE",FACE,{"disambiguationData":[OSD([subQ3,sQuery(id+"F11.wireOp",EDGE,"E32")])]})])],"derivedFrom":makeQuery(id+"F20.opExtrude","SWEPT_EDGE",EDGE,{"disambiguationData":[OSD([subQ1,subQ3])]})});}
            var Q32;
            {var subQ0=sQuery(id+"F11.wireOp",EDGE,"E26");var subQ1=sQuery(id+"F11.wireOp",EDGE,"E41");var subQ2=sQuery(id+"F11.wireOp",EDGE,"E29");var subQ3=sQuery(id+"F11.wireOp",EDGE,"E32");Q32=makeQuery(id+"F20.boolean.opBoolean","COPY",EDGE,{"disambiguationData":[topologyDisambiguationEdgeConnected([makeQuery(id+"F19.boolean.opBoolean","COPY",FACE,{"disambiguationData":[TD([makeQuery(id+"F19.opExtrude","CAP_FACE",FACE,{"disambiguationData":[OSD([subQ0,subQ2,subQ1])],"isStart":true})])],"derivedFrom":makeQuery(id+"F19.opExtrude","SWEPT_FACE",FACE,{"disambiguationData":[OSD([subQ2])]})}),makeQuery(id+"F20.opExtrude","SWEPT_FACE",FACE,{"disambiguationData":[OSD([subQ2])]}),makeQuery(id+"F20.opExtrude","SWEPT_FACE",FACE,{"disambiguationData":[OSD([sQuery(id+"F11.wireOp",EDGE,"E31"),subQ3])]})])],"derivedFrom":makeQuery(id+"F20.opExtrude","SWEPT_EDGE",EDGE,{"disambiguationData":[OSD([subQ2,subQ3])]})});}
            var Q33;
            {var subQ0=sQuery(id+"F11.wireOp",EDGE,"E29");Q33=makeQuery(id+"F20.boolean.opBoolean","MERGE",EDGE,{"derivedFrom":[makeQuery(id+"F19.boolean.opBoolean","COPY",EDGE,{"derivedFrom":makeQuery(id+"F19.opExtrude","CAP_EDGE",EDGE,{"disambiguationData":[OSD([subQ0])],"isStart":true})}),makeQuery(id+"F20.opExtrude","CAP_EDGE",EDGE,{"disambiguationData":[OSD([subQ0])],"isStart":true})]});}
            var Q34;
            {var subQ0=sQuery(id+"F11.wireOp",EDGE,"E23");var subQ1=sQuery(id+"F11.wireOp",EDGE,"E17");Q34=makeQuery(id+"F19.boolean.opBoolean","COPY",EDGE,{"disambiguationData":[TD([makeQuery(id+"F19.opExtrude","CAP_FACE",FACE,{"disambiguationData":[OSD([subQ1,subQ0,sQuery(id+"F11.wireOp",EDGE,"E39")])],"isStart":true})])],"derivedFrom":makeQuery(id+"F19.opExtrude","SWEPT_EDGE",EDGE,{"disambiguationData":[OSD([subQ1,subQ0])]})});}
            var Q35;
            {var subQ0=sQuery(id+"F11.wireOp",EDGE,"E39");var subQ1=sQuery(id+"F11.wireOp",EDGE,"E17");var subQ2=sQuery(id+"F11.wireOp",EDGE,"E23");var subQ3=sQuery(id+"F11.wireOp",EDGE,"E22");Q35=makeQuery(id+"F20.boolean.opBoolean","COPY",EDGE,{"disambiguationData":[topologyDisambiguationEdgeConnected([makeQuery(id+"F19.boolean.opBoolean","COPY",FACE,{"disambiguationData":[TD([makeQuery(id+"F19.opExtrude","CAP_FACE",FACE,{"disambiguationData":[OSD([subQ1,subQ2,subQ0])],"isStart":true})])],"derivedFrom":makeQuery(id+"F19.opExtrude","SWEPT_FACE",FACE,{"disambiguationData":[OSD([subQ2])]})}),makeQuery(id+"F20.opExtrude","SWEPT_FACE",FACE,{"disambiguationData":[OSD([sQuery(id+"F11.wireOp",EDGE,"E21"),subQ3])]}),makeQuery(id+"F20.opExtrude","SWEPT_FACE",FACE,{"disambiguationData":[OSD([subQ2])]})])],"derivedFrom":makeQuery(id+"F20.opExtrude","SWEPT_EDGE",EDGE,{"disambiguationData":[OSD([subQ3,subQ2])]})});}
            var Q36;
            {var subQ0=sQuery(id+"F11.wireOp",EDGE,"E18");var subQ1=sQuery(id+"F11.wireOp",EDGE,"E19");Q36=makeQuery(id+"F19.boolean.opBoolean","COPY",EDGE,{"disambiguationData":[TD([makeQuery(id+"F19.opExtrude","CAP_FACE",FACE,{"disambiguationData":[OSD([subQ0,subQ1,sQuery(id+"F11.wireOp",EDGE,"E38")])],"isStart":true})])],"derivedFrom":makeQuery(id+"F19.opExtrude","SWEPT_EDGE",EDGE,{"disambiguationData":[OSD([subQ0,subQ1])]})});}
            var Q37;
            {var subQ0=sQuery(id+"F11.wireOp",EDGE,"E18");var subQ1=sQuery(id+"F11.wireOp",EDGE,"E38");var subQ2=sQuery(id+"F11.wireOp",EDGE,"E19");var subQ3=sQuery(id+"F11.wireOp",EDGE,"E21");Q37=makeQuery(id+"F20.boolean.opBoolean","COPY",EDGE,{"disambiguationData":[topologyDisambiguationEdgeConnected([makeQuery(id+"F19.boolean.opBoolean","COPY",FACE,{"disambiguationData":[TD([makeQuery(id+"F19.opExtrude","CAP_FACE",FACE,{"disambiguationData":[OSD([subQ0,subQ2,subQ1])],"isStart":true})])],"derivedFrom":makeQuery(id+"F19.opExtrude","SWEPT_FACE",FACE,{"disambiguationData":[OSD([subQ2])]})}),makeQuery(id+"F20.opExtrude","SWEPT_FACE",FACE,{"disambiguationData":[OSD([subQ2])]}),makeQuery(id+"F20.opExtrude","SWEPT_FACE",FACE,{"disambiguationData":[OSD([subQ3,sQuery(id+"F11.wireOp",EDGE,"E22")])]})])],"derivedFrom":makeQuery(id+"F20.opExtrude","SWEPT_EDGE",EDGE,{"disambiguationData":[OSD([subQ2,subQ3])]})});}
            var Q38;
            Q38=makeQuery(id+"F20.boolean.opBoolean","COPY",EDGE,{"derivedFrom":makeQuery(id+"F20.opExtrude","CAP_EDGE",EDGE,{"disambiguationData":[OSD([sQuery(id+"F11.wireOp",EDGE,"E21"),sQuery(id+"F11.wireOp",EDGE,"E22")])],"isStart":true})});
            var Q39;
            {var subQ0=sQuery(id+"F11.wireOp",EDGE,"E19");Q39=makeQuery(id+"F20.boolean.opBoolean","MERGE",EDGE,{"derivedFrom":[makeQuery(id+"F19.boolean.opBoolean","COPY",EDGE,{"derivedFrom":makeQuery(id+"F19.opExtrude","CAP_EDGE",EDGE,{"disambiguationData":[OSD([subQ0])],"isStart":true})}),makeQuery(id+"F20.opExtrude","CAP_EDGE",EDGE,{"disambiguationData":[OSD([subQ0])],"isStart":true})]});}
            var Q40;
            {var subQ0=sQuery(id+"F11.wireOp",EDGE,"E18");var subQ1=sQuery(id+"F11.wireOp",EDGE,"E17");Q40=makeQuery(id+"F20.boolean.opBoolean","MERGE",EDGE,{"derivedFrom":[makeQuery(id+"F19.boolean.opBoolean","COPY",EDGE,{"derivedFrom":makeQuery(id+"F19.opExtrude","CAP_EDGE",EDGE,{"disambiguationData":[OSD([subQ1])],"isStart":true})}),makeQuery(id+"F19.boolean.opBoolean","COPY",EDGE,{"derivedFrom":makeQuery(id+"F19.opExtrude","CAP_EDGE",EDGE,{"disambiguationData":[OSD([subQ0])],"isStart":true})}),makeQuery(id+"F20.opExtrude","CAP_EDGE",EDGE,{"disambiguationData":[OSD([subQ1,subQ0])],"isStart":true})]});}
            var Q41;
            {var subQ0=sQuery(id+"F11.wireOp",EDGE,"E23");Q41=makeQuery(id+"F20.boolean.opBoolean","MERGE",EDGE,{"derivedFrom":[makeQuery(id+"F19.boolean.opBoolean","COPY",EDGE,{"derivedFrom":makeQuery(id+"F19.opExtrude","CAP_EDGE",EDGE,{"disambiguationData":[OSD([subQ0])],"isStart":true})}),makeQuery(id+"F20.opExtrude","CAP_EDGE",EDGE,{"disambiguationData":[OSD([subQ0])],"isStart":true})]});}
            var Q42;
            {var subQ0=sQuery(id+"F7.wireOp",EDGE,"E4.right");var subQ1=sQuery(id+"F7.wireOp",EDGE,"E4.left");var subQ2=sQuery(id+"F7.wireOp",EDGE,"E4.top");var subQ3=sQuery(id+"F7.wireOp",EDGE,"E4.bottom");var subQ4=sQuery(id+"F7.wireOp",EDGE,"E3");var subQ5=sQuery(id+"F11.wireOp",EDGE,"E23");var subQ6=sQuery(id+"F11.wireOp",EDGE,"E17");Q42=makeQuery(id+"F19.boolean.opBoolean","COPY",EDGE,{"disambiguationData":[TD([makeQuery(id+"F13.opExtrude","CAP_FACE",FACE,{"disambiguationData":[OSD([subQ4,subQ3,subQ2,subQ1,subQ0])],"isStart":true})])],"derivedFrom":makeQuery(id+"F19.opExtrude","SWEPT_EDGE",EDGE,{"disambiguationData":[OSD([subQ6,subQ5])]})});}
            var Q43;
            {var subQ0=sQuery(id+"F7.wireOp",EDGE,"E4.right");var subQ1=sQuery(id+"F7.wireOp",EDGE,"E4.left");var subQ2=sQuery(id+"F7.wireOp",EDGE,"E4.top");var subQ3=sQuery(id+"F7.wireOp",EDGE,"E4.bottom");var subQ4=sQuery(id+"F7.wireOp",EDGE,"E3");var subQ5=sQuery(id+"F11.wireOp",EDGE,"E18");var subQ6=sQuery(id+"F11.wireOp",EDGE,"E19");Q43=makeQuery(id+"F19.boolean.opBoolean","COPY",EDGE,{"disambiguationData":[TD([makeQuery(id+"F13.opExtrude","CAP_FACE",FACE,{"disambiguationData":[OSD([subQ4,subQ3,subQ2,subQ1,subQ0])],"isStart":true})])],"derivedFrom":makeQuery(id+"F19.opExtrude","SWEPT_EDGE",EDGE,{"disambiguationData":[OSD([subQ5,subQ6])]})});}
            var Q44;
            {var subQ0=sQuery(id+"F7.wireOp",EDGE,"E4.right");var subQ1=sQuery(id+"F7.wireOp",EDGE,"E4.left");var subQ2=sQuery(id+"F7.wireOp",EDGE,"E4.top");var subQ3=sQuery(id+"F7.wireOp",EDGE,"E4.bottom");var subQ4=sQuery(id+"F7.wireOp",EDGE,"E3");var subQ5=sQuery(id+"F11.wireOp",EDGE,"E23");var subQ6=sQuery(id+"F11.wireOp",EDGE,"E22");Q44=makeQuery(id+"F20.boolean.opBoolean","COPY",EDGE,{"disambiguationData":[topologyDisambiguationEdgeConnected([makeQuery(id+"F19.boolean.opBoolean","COPY",FACE,{"disambiguationData":[TD([makeQuery(id+"F13.opExtrude","CAP_FACE",FACE,{"disambiguationData":[OSD([subQ4,subQ3,subQ2,subQ1,subQ0])],"isStart":true})])],"derivedFrom":makeQuery(id+"F19.opExtrude","SWEPT_FACE",FACE,{"disambiguationData":[OSD([subQ5])]})}),makeQuery(id+"F20.opExtrude","SWEPT_FACE",FACE,{"disambiguationData":[OSD([sQuery(id+"F11.wireOp",EDGE,"E21"),subQ6])]}),makeQuery(id+"F20.opExtrude","SWEPT_FACE",FACE,{"disambiguationData":[OSD([subQ5])]})])],"derivedFrom":makeQuery(id+"F20.opExtrude","SWEPT_EDGE",EDGE,{"disambiguationData":[OSD([subQ6,subQ5])]})});}
            var Q45;
            {var subQ0=sQuery(id+"F7.wireOp",EDGE,"E4.right");var subQ1=sQuery(id+"F7.wireOp",EDGE,"E4.left");var subQ2=sQuery(id+"F7.wireOp",EDGE,"E4.top");var subQ3=sQuery(id+"F7.wireOp",EDGE,"E4.bottom");var subQ4=sQuery(id+"F7.wireOp",EDGE,"E3");var subQ5=sQuery(id+"F11.wireOp",EDGE,"E19");var subQ6=sQuery(id+"F11.wireOp",EDGE,"E21");Q45=makeQuery(id+"F20.boolean.opBoolean","COPY",EDGE,{"disambiguationData":[topologyDisambiguationEdgeConnected([makeQuery(id+"F19.boolean.opBoolean","COPY",FACE,{"disambiguationData":[TD([makeQuery(id+"F13.opExtrude","CAP_FACE",FACE,{"disambiguationData":[OSD([subQ4,subQ3,subQ2,subQ1,subQ0])],"isStart":true})])],"derivedFrom":makeQuery(id+"F19.opExtrude","SWEPT_FACE",FACE,{"disambiguationData":[OSD([subQ5])]})}),makeQuery(id+"F20.opExtrude","SWEPT_FACE",FACE,{"disambiguationData":[OSD([subQ5])]}),makeQuery(id+"F20.opExtrude","SWEPT_FACE",FACE,{"disambiguationData":[OSD([subQ6,sQuery(id+"F11.wireOp",EDGE,"E22")])]})])],"derivedFrom":makeQuery(id+"F20.opExtrude","SWEPT_EDGE",EDGE,{"disambiguationData":[OSD([subQ5,subQ6])]})});}
            var Q46;
            {var subQ0=sQuery(id+"F8.wireOp",EDGE,"E7.right");var subQ1=sQuery(id+"F8.wireOp",EDGE,"E7.left");var subQ2=sQuery(id+"F8.wireOp",EDGE,"E7.top");var subQ3=sQuery(id+"F8.wireOp",EDGE,"E7.bottom");var subQ4=sQuery(id+"F8.wireOp",EDGE,"E6");var subQ5=sQuery(id+"F11.wireOp",EDGE,"E18");var subQ6=sQuery(id+"F11.wireOp",EDGE,"E19");Q46=makeQuery(id+"F19.boolean.opBoolean","COPY",EDGE,{"disambiguationData":[TD([makeQuery(id+"F14.opExtrude","CAP_FACE",FACE,{"disambiguationData":[OSD([subQ4,subQ3,subQ2,subQ1,subQ0])],"isStart":true})])],"derivedFrom":makeQuery(id+"F19.opExtrude","SWEPT_EDGE",EDGE,{"disambiguationData":[OSD([subQ5,subQ6])]})});}
            var Q47;
            {var subQ0=sQuery(id+"F8.wireOp",EDGE,"E7.right");var subQ1=sQuery(id+"F8.wireOp",EDGE,"E7.left");var subQ2=sQuery(id+"F8.wireOp",EDGE,"E7.top");var subQ3=sQuery(id+"F8.wireOp",EDGE,"E7.bottom");var subQ4=sQuery(id+"F8.wireOp",EDGE,"E6");var subQ5=sQuery(id+"F11.wireOp",EDGE,"E19");var subQ6=sQuery(id+"F11.wireOp",EDGE,"E21");Q47=makeQuery(id+"F20.boolean.opBoolean","COPY",EDGE,{"disambiguationData":[topologyDisambiguationEdgeConnected([makeQuery(id+"F19.boolean.opBoolean","COPY",FACE,{"disambiguationData":[TD([makeQuery(id+"F14.opExtrude","CAP_FACE",FACE,{"disambiguationData":[OSD([subQ4,subQ3,subQ2,subQ1,subQ0])],"isStart":true})])],"derivedFrom":makeQuery(id+"F19.opExtrude","SWEPT_FACE",FACE,{"disambiguationData":[OSD([subQ5])]})}),makeQuery(id+"F20.opExtrude","SWEPT_FACE",FACE,{"disambiguationData":[OSD([subQ5])]}),makeQuery(id+"F20.opExtrude","SWEPT_FACE",FACE,{"disambiguationData":[OSD([subQ6,sQuery(id+"F11.wireOp",EDGE,"E22")])]})])],"derivedFrom":makeQuery(id+"F20.opExtrude","SWEPT_EDGE",EDGE,{"disambiguationData":[OSD([subQ5,subQ6])]})});}
            var Q48;
            {var subQ0=sQuery(id+"F8.wireOp",EDGE,"E7.right");var subQ1=sQuery(id+"F8.wireOp",EDGE,"E7.left");var subQ2=sQuery(id+"F8.wireOp",EDGE,"E7.top");var subQ3=sQuery(id+"F8.wireOp",EDGE,"E7.bottom");var subQ4=sQuery(id+"F8.wireOp",EDGE,"E6");var subQ5=sQuery(id+"F11.wireOp",EDGE,"E23");var subQ6=sQuery(id+"F11.wireOp",EDGE,"E22");Q48=makeQuery(id+"F20.boolean.opBoolean","COPY",EDGE,{"disambiguationData":[topologyDisambiguationEdgeConnected([makeQuery(id+"F19.boolean.opBoolean","COPY",FACE,{"disambiguationData":[TD([makeQuery(id+"F14.opExtrude","CAP_FACE",FACE,{"disambiguationData":[OSD([subQ4,subQ3,subQ2,subQ1,subQ0])],"isStart":true})])],"derivedFrom":makeQuery(id+"F19.opExtrude","SWEPT_FACE",FACE,{"disambiguationData":[OSD([subQ5])]})}),makeQuery(id+"F20.opExtrude","SWEPT_FACE",FACE,{"disambiguationData":[OSD([sQuery(id+"F11.wireOp",EDGE,"E21"),subQ6])]}),makeQuery(id+"F20.opExtrude","SWEPT_FACE",FACE,{"disambiguationData":[OSD([subQ5])]})])],"derivedFrom":makeQuery(id+"F20.opExtrude","SWEPT_EDGE",EDGE,{"disambiguationData":[OSD([subQ6,subQ5])]})});}
            var Q49;
            {var subQ0=sQuery(id+"F8.wireOp",EDGE,"E7.right");var subQ1=sQuery(id+"F8.wireOp",EDGE,"E7.left");var subQ2=sQuery(id+"F8.wireOp",EDGE,"E7.top");var subQ3=sQuery(id+"F8.wireOp",EDGE,"E7.bottom");var subQ4=sQuery(id+"F8.wireOp",EDGE,"E6");var subQ5=sQuery(id+"F11.wireOp",EDGE,"E17");var subQ6=sQuery(id+"F11.wireOp",EDGE,"E23");Q49=makeQuery(id+"F19.boolean.opBoolean","COPY",EDGE,{"disambiguationData":[TD([makeQuery(id+"F14.opExtrude","CAP_FACE",FACE,{"disambiguationData":[OSD([subQ4,subQ3,subQ2,subQ1,subQ0])],"isStart":true})])],"derivedFrom":makeQuery(id+"F19.opExtrude","SWEPT_EDGE",EDGE,{"disambiguationData":[OSD([subQ5,subQ6])]})});}
            var Q50;
            {var subQ0=sQuery(id+"F11.wireOp",EDGE,"E17");var subQ1=sQuery(id+"F11.wireOp",EDGE,"E23");Q50=makeQuery(id+"F19.boolean.opBoolean","COPY",EDGE,{"disambiguationData":[TD([makeQuery(id+"F19.opExtrude","CAP_FACE",FACE,{"disambiguationData":[OSD([subQ0,subQ1,sQuery(id+"F11.wireOp",EDGE,"E39")])],"isStart":false})])],"derivedFrom":makeQuery(id+"F19.opExtrude","SWEPT_EDGE",EDGE,{"disambiguationData":[OSD([subQ0,subQ1])]})});}
            var Q51;
            {var subQ0=sQuery(id+"F11.wireOp",EDGE,"E17");var subQ1=sQuery(id+"F11.wireOp",EDGE,"E39");var subQ2=sQuery(id+"F11.wireOp",EDGE,"E23");var subQ3=sQuery(id+"F11.wireOp",EDGE,"E22");Q51=makeQuery(id+"F20.boolean.opBoolean","COPY",EDGE,{"disambiguationData":[topologyDisambiguationEdgeConnected([makeQuery(id+"F19.boolean.opBoolean","COPY",FACE,{"disambiguationData":[TD([makeQuery(id+"F19.opExtrude","CAP_FACE",FACE,{"disambiguationData":[OSD([subQ0,subQ2,subQ1])],"isStart":false})])],"derivedFrom":makeQuery(id+"F19.opExtrude","SWEPT_FACE",FACE,{"disambiguationData":[OSD([subQ2])]})}),makeQuery(id+"F20.opExtrude","SWEPT_FACE",FACE,{"disambiguationData":[OSD([sQuery(id+"F11.wireOp",EDGE,"E21"),subQ3])]}),makeQuery(id+"F20.opExtrude","SWEPT_FACE",FACE,{"disambiguationData":[OSD([subQ2])]})])],"derivedFrom":makeQuery(id+"F20.opExtrude","SWEPT_EDGE",EDGE,{"disambiguationData":[OSD([subQ3,subQ2])]})});}
            var Q52;
            {var subQ0=sQuery(id+"F11.wireOp",EDGE,"E18");var subQ1=sQuery(id+"F11.wireOp",EDGE,"E38");var subQ2=sQuery(id+"F11.wireOp",EDGE,"E19");var subQ3=sQuery(id+"F11.wireOp",EDGE,"E21");Q52=makeQuery(id+"F20.boolean.opBoolean","COPY",EDGE,{"disambiguationData":[topologyDisambiguationEdgeConnected([makeQuery(id+"F19.boolean.opBoolean","COPY",FACE,{"disambiguationData":[TD([makeQuery(id+"F19.opExtrude","CAP_FACE",FACE,{"disambiguationData":[OSD([subQ0,subQ2,subQ1])],"isStart":false})])],"derivedFrom":makeQuery(id+"F19.opExtrude","SWEPT_FACE",FACE,{"disambiguationData":[OSD([subQ2])]})}),makeQuery(id+"F20.opExtrude","SWEPT_FACE",FACE,{"disambiguationData":[OSD([subQ2])]}),makeQuery(id+"F20.opExtrude","SWEPT_FACE",FACE,{"disambiguationData":[OSD([subQ3,sQuery(id+"F11.wireOp",EDGE,"E22")])]})])],"derivedFrom":makeQuery(id+"F20.opExtrude","SWEPT_EDGE",EDGE,{"disambiguationData":[OSD([subQ2,subQ3])]})});}
            var Q53;
            {var subQ0=sQuery(id+"F11.wireOp",EDGE,"E18");var subQ1=sQuery(id+"F11.wireOp",EDGE,"E19");Q53=makeQuery(id+"F19.boolean.opBoolean","COPY",EDGE,{"disambiguationData":[TD([makeQuery(id+"F19.opExtrude","CAP_FACE",FACE,{"disambiguationData":[OSD([subQ0,subQ1,sQuery(id+"F11.wireOp",EDGE,"E38")])],"isStart":false})])],"derivedFrom":makeQuery(id+"F19.opExtrude","SWEPT_EDGE",EDGE,{"disambiguationData":[OSD([subQ0,subQ1])]})});}
            var Q54;
            Q54=makeQuery(id+"F19.boolean.opBoolean","COPY",EDGE,{"derivedFrom":makeQuery(id+"F19.opExtrude","CAP_EDGE",EDGE,{"disambiguationData":[OSD([sQuery(id+"F11.wireOp",EDGE,"E19")])],"isStart":false})});
            var Q55;
            Q55=makeQuery(id+"F19.boolean.opBoolean","COPY",EDGE,{"derivedFrom":makeQuery(id+"F19.opExtrude","CAP_EDGE",EDGE,{"disambiguationData":[OSD([sQuery(id+"F11.wireOp",EDGE,"E18")])],"isStart":false})});
            var Q56;
            Q56=makeQuery(id+"F19.boolean.opBoolean","COPY",EDGE,{"derivedFrom":makeQuery(id+"F19.opExtrude","CAP_EDGE",EDGE,{"disambiguationData":[OSD([sQuery(id+"F11.wireOp",EDGE,"E23")])],"isStart":false})});
            var Q57;
            Q57=makeQuery(id+"F19.boolean.opBoolean","COPY",EDGE,{"derivedFrom":makeQuery(id+"F19.opExtrude","CAP_EDGE",EDGE,{"disambiguationData":[OSD([sQuery(id+"F11.wireOp",EDGE,"E17")])],"isStart":false})});
            var Q58;
            {var subQ0=sQuery(id+"F11.wireOp",EDGE,"E18");var subQ1=sQuery(id+"F11.wireOp",EDGE,"E38");var subQ2=sQuery(id+"F11.wireOp",EDGE,"E19");Q58=makeQuery(id+"F20.boolean.opBoolean","COPY",EDGE,{"disambiguationData":[topologyDisambiguationEdgeConnected([makeQuery(id+"F19.boolean.opBoolean","COPY",FACE,{"disambiguationData":[TD([makeQuery(id+"F19.opExtrude","CAP_FACE",FACE,{"disambiguationData":[OSD([subQ0,subQ2,subQ1])],"isStart":false})])],"derivedFrom":makeQuery(id+"F19.opExtrude","SWEPT_FACE",FACE,{"disambiguationData":[OSD([subQ2])]})}),makeQuery(id+"F20.opExtrude","SWEPT_FACE",FACE,{"disambiguationData":[OSD([subQ2])]}),makeQuery(id+"F20.opExtrude","SWEPT_FACE",FACE,{"disambiguationData":[OSD([subQ1])]})])],"derivedFrom":makeQuery(id+"F20.opExtrude","SWEPT_EDGE",EDGE,{"disambiguationData":[OSD([subQ2,subQ1])]})});}
            var Q59;
            {var subQ1=sQuery(id+"F11.wireOp",EDGE,"E39");var subQ2=sQuery(id+"F11.wireOp",EDGE,"E23");var subQ3=sQuery(id+"F11.wireOp",EDGE,"E17");var subQ4=sQuery(id+"F11.wireOp",EDGE,"E38");var subQ5=sQuery(id+"F11.wireOp",EDGE,"E19");var subQ6=sQuery(id+"F11.wireOp",EDGE,"E18");Q59=makeQuery(id+"F20.boolean.opBoolean","COPY",EDGE,{"disambiguationData":[topologyDisambiguationEdgeConnected([makeQuery(id+"F19.boolean.opBoolean","COPY",FACE,{"disambiguationData":[TD([makeQuery(id+"F19.opExtrude","CAP_FACE",FACE,{"disambiguationData":[OSD([subQ3,subQ2,subQ1])],"isStart":false})])],"derivedFrom":makeQuery(id+"F19.opExtrude","SWEPT_FACE",FACE,{"disambiguationData":[OSD([subQ3])]})}),makeQuery(id+"F19.boolean.opBoolean","COPY",FACE,{"disambiguationData":[TD([makeQuery(id+"F19.opExtrude","CAP_FACE",FACE,{"disambiguationData":[OSD([subQ6,subQ5,subQ4])],"isStart":false})])],"derivedFrom":makeQuery(id+"F19.opExtrude","SWEPT_FACE",FACE,{"disambiguationData":[OSD([subQ6])]})}),makeQuery(id+"F20.opExtrude","SWEPT_FACE",FACE,{"disambiguationData":[OSD([subQ3,subQ6])]}),makeQuery(id+"F20.opExtrude","SWEPT_FACE",FACE,{"disambiguationData":[OSD([subQ4])]})])],"derivedFrom":makeQuery(id+"F20.opExtrude","SWEPT_EDGE",EDGE,{"disambiguationData":[OSD([subQ6,subQ4])]})});}
            var Q60;
            {var subQ1=sQuery(id+"F11.wireOp",EDGE,"E39");var subQ2=sQuery(id+"F11.wireOp",EDGE,"E23");var subQ3=sQuery(id+"F11.wireOp",EDGE,"E17");var subQ4=sQuery(id+"F11.wireOp",EDGE,"E38");var subQ5=sQuery(id+"F11.wireOp",EDGE,"E19");var subQ6=sQuery(id+"F11.wireOp",EDGE,"E18");Q60=makeQuery(id+"F20.boolean.opBoolean","COPY",EDGE,{"disambiguationData":[topologyDisambiguationEdgeConnected([makeQuery(id+"F19.boolean.opBoolean","COPY",FACE,{"disambiguationData":[TD([makeQuery(id+"F19.opExtrude","CAP_FACE",FACE,{"disambiguationData":[OSD([subQ3,subQ2,subQ1])],"isStart":false})])],"derivedFrom":makeQuery(id+"F19.opExtrude","SWEPT_FACE",FACE,{"disambiguationData":[OSD([subQ3])]})}),makeQuery(id+"F19.boolean.opBoolean","COPY",FACE,{"disambiguationData":[TD([makeQuery(id+"F19.opExtrude","CAP_FACE",FACE,{"disambiguationData":[OSD([subQ6,subQ5,subQ4])],"isStart":false})])],"derivedFrom":makeQuery(id+"F19.opExtrude","SWEPT_FACE",FACE,{"disambiguationData":[OSD([subQ6])]})}),makeQuery(id+"F20.opExtrude","SWEPT_FACE",FACE,{"disambiguationData":[OSD([subQ3,subQ6])]}),makeQuery(id+"F20.opExtrude","SWEPT_FACE",FACE,{"disambiguationData":[OSD([subQ1])]})])],"derivedFrom":makeQuery(id+"F20.opExtrude","SWEPT_EDGE",EDGE,{"disambiguationData":[OSD([subQ3,subQ1])]})});}
            var Q61;
            {var subQ0=sQuery(id+"F11.wireOp",EDGE,"E17");var subQ1=sQuery(id+"F11.wireOp",EDGE,"E39");var subQ2=sQuery(id+"F11.wireOp",EDGE,"E23");Q61=makeQuery(id+"F20.boolean.opBoolean","COPY",EDGE,{"disambiguationData":[topologyDisambiguationEdgeConnected([makeQuery(id+"F19.boolean.opBoolean","COPY",FACE,{"disambiguationData":[TD([makeQuery(id+"F19.opExtrude","CAP_FACE",FACE,{"disambiguationData":[OSD([subQ0,subQ2,subQ1])],"isStart":false})])],"derivedFrom":makeQuery(id+"F19.opExtrude","SWEPT_FACE",FACE,{"disambiguationData":[OSD([subQ2])]})}),makeQuery(id+"F20.opExtrude","SWEPT_FACE",FACE,{"disambiguationData":[OSD([subQ2])]}),makeQuery(id+"F20.opExtrude","SWEPT_FACE",FACE,{"disambiguationData":[OSD([subQ1])]})])],"derivedFrom":makeQuery(id+"F20.opExtrude","SWEPT_EDGE",EDGE,{"disambiguationData":[OSD([subQ2,subQ1])]})});}
            var Q62;
            {var subQ0=sQuery(id+"F11.wireOp",EDGE,"E18");var subQ1=sQuery(id+"F11.wireOp",EDGE,"E38");Q62=makeQuery(id+"F20.boolean.opBoolean","COPY",EDGE,{"disambiguationData":[topologyDisambiguationEdgeConnected([makeQuery(id+"F20.opExtrude","SWEPT_FACE",FACE,{"disambiguationData":[OSD([sQuery(id+"F11.wireOp",EDGE,"E17"),subQ0])]}),makeQuery(id+"F20.opExtrude","SWEPT_FACE",FACE,{"disambiguationData":[OSD([subQ1])]})])],"derivedFrom":makeQuery(id+"F20.opExtrude","SWEPT_EDGE",EDGE,{"disambiguationData":[OSD([subQ0,subQ1])]})});}
            var Q63;
            {var subQ0=sQuery(id+"F11.wireOp",EDGE,"E19");var subQ1=sQuery(id+"F11.wireOp",EDGE,"E38");Q63=makeQuery(id+"F20.boolean.opBoolean","COPY",EDGE,{"disambiguationData":[topologyDisambiguationEdgeConnected([makeQuery(id+"F20.opExtrude","SWEPT_FACE",FACE,{"disambiguationData":[OSD([subQ0])]}),makeQuery(id+"F20.opExtrude","SWEPT_FACE",FACE,{"disambiguationData":[OSD([subQ1])]})])],"derivedFrom":makeQuery(id+"F20.opExtrude","SWEPT_EDGE",EDGE,{"disambiguationData":[OSD([subQ0,subQ1])]})});}
            var Q64;
            {var subQ0=sQuery(id+"F11.wireOp",EDGE,"E17");var subQ1=sQuery(id+"F11.wireOp",EDGE,"E39");Q64=makeQuery(id+"F20.boolean.opBoolean","COPY",EDGE,{"disambiguationData":[topologyDisambiguationEdgeConnected([makeQuery(id+"F20.opExtrude","SWEPT_FACE",FACE,{"disambiguationData":[OSD([subQ0,sQuery(id+"F11.wireOp",EDGE,"E18")])]}),makeQuery(id+"F20.opExtrude","SWEPT_FACE",FACE,{"disambiguationData":[OSD([subQ1])]})])],"derivedFrom":makeQuery(id+"F20.opExtrude","SWEPT_EDGE",EDGE,{"disambiguationData":[OSD([subQ0,subQ1])]})});}
            var Q65;
            {var subQ0=sQuery(id+"F11.wireOp",EDGE,"E23");var subQ1=sQuery(id+"F11.wireOp",EDGE,"E39");Q65=makeQuery(id+"F20.boolean.opBoolean","COPY",EDGE,{"disambiguationData":[topologyDisambiguationEdgeConnected([makeQuery(id+"F20.opExtrude","SWEPT_FACE",FACE,{"disambiguationData":[OSD([subQ0])]}),makeQuery(id+"F20.opExtrude","SWEPT_FACE",FACE,{"disambiguationData":[OSD([subQ1])]})])],"derivedFrom":makeQuery(id+"F20.opExtrude","SWEPT_EDGE",EDGE,{"disambiguationData":[OSD([subQ0,subQ1])]})});}
            var Q66;
            {var subQ0=sQuery(id+"F11.wireOp",EDGE,"E22");var subQ1=sQuery(id+"F11.wireOp",EDGE,"E23");Q66=makeQuery(id+"F20.boolean.opBoolean","COPY",EDGE,{"disambiguationData":[topologyDisambiguationEdgeConnected([makeQuery(id+"F20.opExtrude","SWEPT_FACE",FACE,{"disambiguationData":[OSD([sQuery(id+"F11.wireOp",EDGE,"E21"),subQ0])]}),makeQuery(id+"F20.opExtrude","SWEPT_FACE",FACE,{"disambiguationData":[OSD([subQ1])]})])],"derivedFrom":makeQuery(id+"F20.opExtrude","SWEPT_EDGE",EDGE,{"disambiguationData":[OSD([subQ0,subQ1])]})});}
            var Q67;
            {var subQ0=sQuery(id+"F11.wireOp",EDGE,"E19");var subQ1=sQuery(id+"F11.wireOp",EDGE,"E21");Q67=makeQuery(id+"F20.boolean.opBoolean","COPY",EDGE,{"disambiguationData":[topologyDisambiguationEdgeConnected([makeQuery(id+"F20.opExtrude","SWEPT_FACE",FACE,{"disambiguationData":[OSD([subQ0])]}),makeQuery(id+"F20.opExtrude","SWEPT_FACE",FACE,{"disambiguationData":[OSD([subQ1,sQuery(id+"F11.wireOp",EDGE,"E22")])]})])],"derivedFrom":makeQuery(id+"F20.opExtrude","SWEPT_EDGE",EDGE,{"disambiguationData":[OSD([subQ0,subQ1])]})});}
            fillet(context, id + "F40", {"entities" : qUnion([Q0, Q1, Q2, Q3, Q4, Q5, Q6, Q7, Q8, Q9, Q10, Q11, Q12, Q13, Q14, Q15, Q16, Q17, Q18, Q19, Q20, Q21, Q22, Q23, Q24, Q25, Q26, Q27, Q28, Q29, Q30, Q31, Q32, Q33, Q34, Q35, Q36, Q37, Q38, Q39, Q40, Q41, Q42, Q43, Q44, Q45, Q46, Q47, Q48, Q49, Q50, Q51, Q52, Q53, Q54, Q55, Q56, Q57, Q58, Q59, Q60, Q61, Q62, Q63, Q64, Q65, Q66, Q67]), "radius" : 3 * mm, "tangentPropagation" : true, "allowEdgeOverflow" : false});
        }
    });
